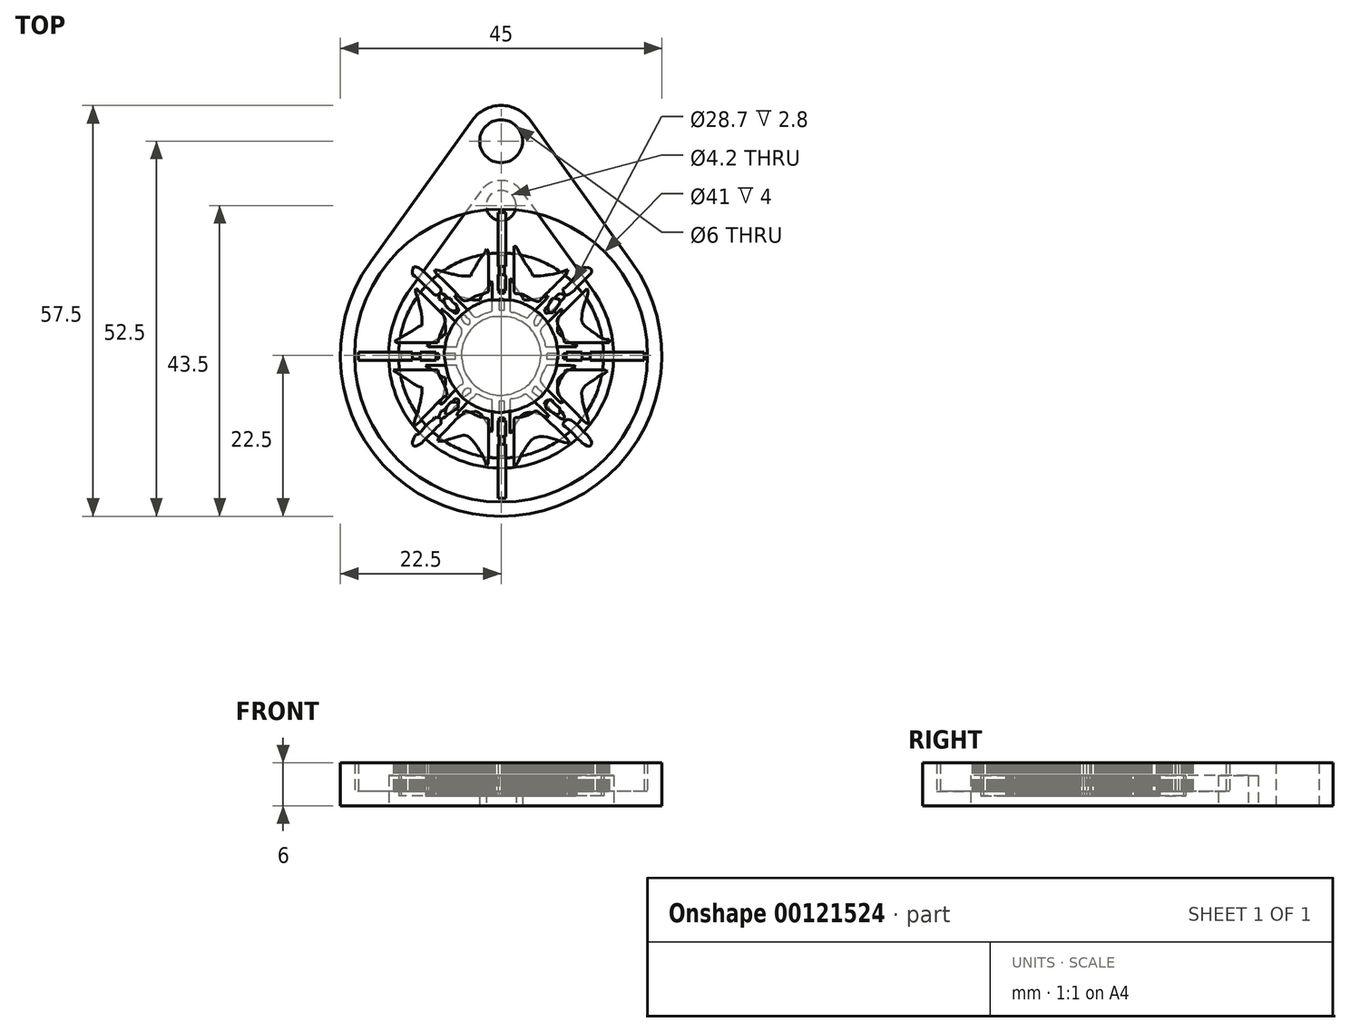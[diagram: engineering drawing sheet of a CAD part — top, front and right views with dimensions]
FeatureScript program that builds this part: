
annotation { "Feature Type Name" : "Feature", "Feature Type Description" : "" }
export const myFeature = defineFeature(function(context is Context, id is Id, definition is map)
    precondition{}
    {
        {
            var Q0;
            Q0=qCreatedBy(makeId("Top.planeOp"),FACE);
            var sketch = newSketch(context, id + "F0", { "sketchPlane" : qUnion([Q0])});
            skCircle(sketch, "E0", {"center": v(0, 0) * mm, "radius": 22.5 * mm});
            skCircle(sketch, "E1", {"center": v(0, 30) * mm, "radius": 5 * mm});
            skCircle(sketch, "E2", {"center": v(0, 30) * mm, "radius": 3 * mm});
            skLineSegment(sketch, "E3", {"start": v(-4.06, 32.92) * mm, "end": v(-18.28, 13.12) * mm});
            skLineSegment(sketch, "E4", {"start": v(4.06, 32.92) * mm, "end": v(18.28, 13.12) * mm});
            skCircle(sketch, "E5.0", {"center": v(0, 0) * mm, "radius": 20.5 * mm});
            skSolve(sketch);
        }
        {
            var Q0;
            Q0=makeQuery(id+"F0.imprint","IMPRINT",FACE,{"disambiguationData":[TD([[makeQuery(id+"F0.imprint","IMPRINT",EDGE,{"derivedFrom":sQuery(id+"F0.wireOp",EDGE,"E5.0")}),-1.0]])]});
            var Q1;
            {var subQ0=sQuery(id+"F0.wireOp",EDGE,"E3");Q1=makeQuery(id+"F0.imprint","IMPRINT",FACE,{"disambiguationData":[TD([[makeQuery(id+"F0.imprint","IMPRINT",EDGE,{"derivedFrom":subQ0}),1.0]])]});}
            var Q2;
            Q2=makeQuery(id+"F0.imprint","IMPRINT",FACE,{"disambiguationData":[TD([[makeQuery(id+"F0.imprint","IMPRINT",EDGE,{"derivedFrom":sQuery(id+"F0.wireOp",EDGE,"E2")}),-1.0]])]});
            extrude(context, id + "F1", {"entities" : qUnion([Q0, Q1, Q2]), "depth" : 6 * mm});
        }
        {
            var Q0;
            Q0=makeQuery(id+"F0.imprint","IMPRINT",FACE,{"disambiguationData":[TD([[makeQuery(id+"F0.imprint","IMPRINT",EDGE,{"derivedFrom":sQuery(id+"F0.wireOp",EDGE,"E5.0")}),1.0]])]});
            extrude(context, id + "F2", {"entities" : qUnion([Q0]), "operationType" : NewBodyOperationType.ADD, "depth" : 2 * mm});
        }
        {
            var Q0;
            Q0=makeQuery(id+"F2.opExtrude","CAP_FACE",FACE,{"disambiguationData":[OSD([sQuery(id+"F0.wireOp",EDGE,"E5.0")])],"isStart":false});
            var sketch = newSketch(context, id + "F3", { "sketchPlane" : qUnion([Q0])});
            skLineSegment(sketch, "E6", {"start": v(-0.44, 20) * mm, "end": v(-0.44, 12.44) * mm});
            skLineSegment(sketch, "E7", {"start": v(-0.44, 12.44) * mm, "end": v(0.67, 12.44) * mm});
            skLineSegment(sketch, "E8", {"start": v(0.67, 12.44) * mm, "end": v(0.67, 20) * mm});
            skLineSegment(sketch, "E9", {"start": v(0.67, 20) * mm, "end": v(-0.44, 20) * mm});
            skLineSegment(sketch, "E10", {"start": v(1.78, 15.33) * mm, "end": v(1.78, 8.89) * mm});
            skLineSegment(sketch, "E11", {"start": v(1.78, 8.89) * mm, "end": v(2, 8.67) * mm});
            skLineSegment(sketch, "E12", {"start": v(2, 8.67) * mm, "end": v(2.33, 8.66) * mm});
            skLineSegment(sketch, "E13", {"start": v(2.33, 8.66) * mm, "end": v(2.68, 8.62) * mm});
            skLineSegment(sketch, "E14", {"start": v(2.68, 8.62) * mm, "end": v(2.89, 8.57) * mm});
            skLineSegment(sketch, "E15", {"start": v(2.89, 8.57) * mm, "end": v(3.11, 8.5) * mm});
            skLineSegment(sketch, "E16", {"start": v(3.11, 8.5) * mm, "end": v(3.33, 8.42) * mm});
            skLineSegment(sketch, "E17", {"start": v(3.33, 8.42) * mm, "end": v(3.56, 8.3) * mm});
            skLineSegment(sketch, "E18", {"start": v(3.56, 8.3) * mm, "end": v(4, 8.04) * mm});
            skLineSegment(sketch, "E19", {"start": v(4, 8.04) * mm, "end": v(4.22, 7.91) * mm});
            skLineSegment(sketch, "E20", {"start": v(4.22, 7.91) * mm, "end": v(4.44, 7.8) * mm});
            skLineSegment(sketch, "E21", {"start": v(4.44, 7.8) * mm, "end": v(4.88, 7.65) * mm});
            skLineSegment(sketch, "E22", {"start": v(4.88, 7.65) * mm, "end": v(5, 7.61) * mm});
            skLineSegment(sketch, "E23", {"start": v(5, 7.61) * mm, "end": v(5.33, 7.56) * mm});
            skLineSegment(sketch, "E24", {"start": v(5.33, 7.56) * mm, "end": v(5.61, 7.88) * mm});
            skLineSegment(sketch, "E25", {"start": v(5.61, 7.88) * mm, "end": v(5.86, 8.19) * mm});
            skLineSegment(sketch, "E26", {"start": v(5.86, 8.19) * mm, "end": v(6, 8.35) * mm});
            skLineSegment(sketch, "E27", {"start": v(6, 8.35) * mm, "end": v(6.31, 8.67) * mm});
            skLineSegment(sketch, "E28", {"start": v(6.31, 8.67) * mm, "end": v(6.67, 8.98) * mm});
            skLineSegment(sketch, "E29", {"start": v(6.67, 8.98) * mm, "end": v(6.85, 9.15) * mm});
            skLineSegment(sketch, "E30", {"start": v(6.85, 9.15) * mm, "end": v(7.2, 9.51) * mm});
            skLineSegment(sketch, "E31", {"start": v(7.2, 9.51) * mm, "end": v(7.56, 9.86) * mm});
            skLineSegment(sketch, "E32", {"start": v(7.56, 9.86) * mm, "end": v(7.91, 10.22) * mm});
            skLineSegment(sketch, "E33", {"start": v(7.91, 10.22) * mm, "end": v(8.09, 10.4) * mm});
            skLineSegment(sketch, "E34", {"start": v(8.09, 10.4) * mm, "end": v(8.27, 10.58) * mm});
            skLineSegment(sketch, "E35", {"start": v(8.27, 10.58) * mm, "end": v(8.67, 10.94) * mm});
            skLineSegment(sketch, "E36", {"start": v(8.67, 10.94) * mm, "end": v(8.86, 11.13) * mm});
            skLineSegment(sketch, "E37", {"start": v(8.86, 11.13) * mm, "end": v(9.04, 11.33) * mm});
            skLineSegment(sketch, "E38", {"start": v(9.04, 11.33) * mm, "end": v(9.25, 11.67) * mm});
            skLineSegment(sketch, "E39", {"start": v(9.25, 11.67) * mm, "end": v(9.33, 12) * mm});
            skLineSegment(sketch, "E40", {"start": v(9.33, 12) * mm, "end": v(9, 11.9) * mm});
            skLineSegment(sketch, "E41", {"start": v(9, 11.9) * mm, "end": v(8.88, 11.85) * mm});
            skLineSegment(sketch, "E42", {"start": v(8.88, 11.85) * mm, "end": v(8.65, 11.78) * mm});
            skLineSegment(sketch, "E43", {"start": v(8.65, 11.78) * mm, "end": v(8.22, 11.64) * mm});
            skLineSegment(sketch, "E44", {"start": v(8.22, 11.64) * mm, "end": v(8, 11.59) * mm});
            skLineSegment(sketch, "E45", {"start": v(8, 11.59) * mm, "end": v(7.78, 11.52) * mm});
            skLineSegment(sketch, "E46", {"start": v(7.78, 11.52) * mm, "end": v(7.33, 11.42) * mm});
            skLineSegment(sketch, "E47", {"start": v(7.33, 11.42) * mm, "end": v(6.89, 11.35) * mm});
            skLineSegment(sketch, "E48", {"start": v(6.89, 11.35) * mm, "end": v(6.67, 11.32) * mm});
            skLineSegment(sketch, "E49", {"start": v(6.67, 11.32) * mm, "end": v(6.44, 11.28) * mm});
            skLineSegment(sketch, "E50", {"start": v(6.44, 11.28) * mm, "end": v(6.22, 11.25) * mm});
            skLineSegment(sketch, "E51", {"start": v(6.22, 11.25) * mm, "end": v(6, 11.2) * mm});
            skLineSegment(sketch, "E52", {"start": v(6, 11.2) * mm, "end": v(5.56, 11.13) * mm});
            skLineSegment(sketch, "E53", {"start": v(5.56, 11.13) * mm, "end": v(5.33, 11.12) * mm});
            skLineSegment(sketch, "E54", {"start": v(5.33, 11.12) * mm, "end": v(4.9, 11.11) * mm});
            skLineSegment(sketch, "E55", {"start": v(4.9, 11.11) * mm, "end": v(4.44, 11.11) * mm});
            skLineSegment(sketch, "E56", {"start": v(4.44, 11.11) * mm, "end": v(4.36, 11.44) * mm});
            skLineSegment(sketch, "E57", {"start": v(4.36, 11.44) * mm, "end": v(4.3, 11.57) * mm});
            skLineSegment(sketch, "E58", {"start": v(4.3, 11.57) * mm, "end": v(4.17, 11.8) * mm});
            skLineSegment(sketch, "E59", {"start": v(4.17, 11.8) * mm, "end": v(3.88, 12.22) * mm});
            skLineSegment(sketch, "E60", {"start": v(3.88, 12.22) * mm, "end": v(3.74, 12.43) * mm});
            skLineSegment(sketch, "E61", {"start": v(3.74, 12.43) * mm, "end": v(3.48, 12.8) * mm});
            skLineSegment(sketch, "E62", {"start": v(3.48, 12.8) * mm, "end": v(3.35, 12.98) * mm});
            skLineSegment(sketch, "E63", {"start": v(3.35, 12.98) * mm, "end": v(3.11, 13.35) * mm});
            skLineSegment(sketch, "E64", {"start": v(3.11, 13.35) * mm, "end": v(2.88, 13.78) * mm});
            skLineSegment(sketch, "E65", {"start": v(2.88, 13.78) * mm, "end": v(2.75, 14) * mm});
            skLineSegment(sketch, "E66", {"start": v(2.75, 14) * mm, "end": v(2.5, 14.44) * mm});
            skLineSegment(sketch, "E67", {"start": v(2.5, 14.44) * mm, "end": v(2.3, 14.86) * mm});
            skLineSegment(sketch, "E68", {"start": v(2.3, 14.86) * mm, "end": v(2.22, 15.04) * mm});
            skLineSegment(sketch, "E69", {"start": v(2.22, 15.04) * mm, "end": v(2.1, 15.17) * mm});
            skLineSegment(sketch, "E70", {"start": v(2.1, 15.17) * mm, "end": v(2.04, 15.25) * mm});
            skLineSegment(sketch, "E71", {"start": v(2.04, 15.25) * mm, "end": v(1.78, 15.33) * mm});
            skLineSegment(sketch, "E72", {"start": v(-2, 14.89) * mm, "end": v(-2.22, 14.56) * mm});
            skLineSegment(sketch, "E73", {"start": v(-2.22, 14.56) * mm, "end": v(-2.28, 14.44) * mm});
            skLineSegment(sketch, "E74", {"start": v(-2.28, 14.44) * mm, "end": v(-2.53, 14.05) * mm});
            skLineSegment(sketch, "E75", {"start": v(-2.53, 14.05) * mm, "end": v(-2.8, 13.7) * mm});
            skLineSegment(sketch, "E76", {"start": v(-2.8, 13.7) * mm, "end": v(-3.07, 13.31) * mm});
            skLineSegment(sketch, "E77", {"start": v(-3.07, 13.31) * mm, "end": v(-3.2, 13.1) * mm});
            skLineSegment(sketch, "E78", {"start": v(-3.2, 13.1) * mm, "end": v(-3.32, 12.89) * mm});
            skLineSegment(sketch, "E79", {"start": v(-3.32, 12.89) * mm, "end": v(-3.56, 12.46) * mm});
            skLineSegment(sketch, "E80", {"start": v(-3.56, 12.46) * mm, "end": v(-3.8, 12.09) * mm});
            skLineSegment(sketch, "E81", {"start": v(-3.8, 12.09) * mm, "end": v(-4.02, 11.74) * mm});
            skLineSegment(sketch, "E82", {"start": v(-4.02, 11.74) * mm, "end": v(-4.16, 11.44) * mm});
            skLineSegment(sketch, "E83", {"start": v(-4.16, 11.44) * mm, "end": v(-4.22, 11.11) * mm});
            skLineSegment(sketch, "E84", {"start": v(-4.22, 11.11) * mm, "end": v(-4.9, 11.11) * mm});
            skLineSegment(sketch, "E85", {"start": v(-4.9, 11.11) * mm, "end": v(-5.11, 11.11) * mm});
            skLineSegment(sketch, "E86", {"start": v(-5.11, 11.11) * mm, "end": v(-5.56, 11.13) * mm});
            skLineSegment(sketch, "E87", {"start": v(-5.56, 11.13) * mm, "end": v(-6, 11.2) * mm});
            skLineSegment(sketch, "E88", {"start": v(-6, 11.2) * mm, "end": v(-6.22, 11.25) * mm});
            skLineSegment(sketch, "E89", {"start": v(-6.22, 11.25) * mm, "end": v(-6.67, 11.36) * mm});
            skLineSegment(sketch, "E90", {"start": v(-6.67, 11.36) * mm, "end": v(-6.89, 11.41) * mm});
            skLineSegment(sketch, "E91", {"start": v(-6.89, 11.41) * mm, "end": v(-7.11, 11.48) * mm});
            skLineSegment(sketch, "E92", {"start": v(-7.11, 11.48) * mm, "end": v(-7.33, 11.52) * mm});
            skLineSegment(sketch, "E93", {"start": v(-7.33, 11.52) * mm, "end": v(-7.78, 11.64) * mm});
            skLineSegment(sketch, "E94", {"start": v(-7.78, 11.64) * mm, "end": v(-8, 11.7) * mm});
            skLineSegment(sketch, "E95", {"start": v(-8, 11.7) * mm, "end": v(-8.44, 11.85) * mm});
            skLineSegment(sketch, "E96", {"start": v(-8.44, 11.85) * mm, "end": v(-8.65, 11.9) * mm});
            skLineSegment(sketch, "E97", {"start": v(-8.65, 11.9) * mm, "end": v(-9, 11.98) * mm});
            skLineSegment(sketch, "E98", {"start": v(-9, 11.98) * mm, "end": v(-9.33, 12) * mm});
            skLineSegment(sketch, "E99", {"start": v(-9.33, 12) * mm, "end": v(-9.25, 11.72) * mm});
            skLineSegment(sketch, "E100", {"start": v(-9.25, 11.72) * mm, "end": v(-9.17, 11.63) * mm});
            skLineSegment(sketch, "E101", {"start": v(-9.17, 11.63) * mm, "end": v(-9.04, 11.46) * mm});
            skLineSegment(sketch, "E102", {"start": v(-9.04, 11.46) * mm, "end": v(-8.66, 11.1) * mm});
            skLineSegment(sketch, "E103", {"start": v(-8.66, 11.1) * mm, "end": v(-8.22, 10.67) * mm});
            skLineSegment(sketch, "E104", {"start": v(-8.22, 10.67) * mm, "end": v(-7.78, 10.22) * mm});
            skLineSegment(sketch, "E105", {"start": v(-7.78, 10.22) * mm, "end": v(-7.11, 9.56) * mm});
            skLineSegment(sketch, "E106", {"start": v(-7.11, 9.56) * mm, "end": v(-6.67, 9.11) * mm});
            skLineSegment(sketch, "E107", {"start": v(-6.67, 9.11) * mm, "end": v(-6.45, 8.89) * mm});
            skLineSegment(sketch, "E108", {"start": v(-6.45, 8.89) * mm, "end": v(-6.24, 8.67) * mm});
            skLineSegment(sketch, "E109", {"start": v(-6.24, 8.67) * mm, "end": v(-5.86, 8.23) * mm});
            skLineSegment(sketch, "E110", {"start": v(-5.86, 8.23) * mm, "end": v(-5.7, 8.02) * mm});
            skLineSegment(sketch, "E111", {"start": v(-5.7, 8.02) * mm, "end": v(-5.5, 7.85) * mm});
            skLineSegment(sketch, "E112", {"start": v(-5.5, 7.85) * mm, "end": v(-5.1, 7.65) * mm});
            skLineSegment(sketch, "E113", {"start": v(-5.1, 7.65) * mm, "end": v(-4.67, 7.72) * mm});
            skLineSegment(sketch, "E114", {"start": v(-4.67, 7.72) * mm, "end": v(-4.44, 7.83) * mm});
            skLineSegment(sketch, "E115", {"start": v(-4.44, 7.83) * mm, "end": v(-4, 8.12) * mm});
            skLineSegment(sketch, "E116", {"start": v(-4, 8.12) * mm, "end": v(-3.78, 8.23) * mm});
            skLineSegment(sketch, "E117", {"start": v(-3.78, 8.23) * mm, "end": v(-3.56, 8.34) * mm});
            skLineSegment(sketch, "E118", {"start": v(-3.56, 8.34) * mm, "end": v(-3.11, 8.48) * mm});
            skLineSegment(sketch, "E119", {"start": v(-3.11, 8.48) * mm, "end": v(-2.89, 8.53) * mm});
            skLineSegment(sketch, "E120", {"start": v(-2.89, 8.53) * mm, "end": v(-2.67, 8.6) * mm});
            skLineSegment(sketch, "E121", {"start": v(-2.67, 8.6) * mm, "end": v(-2.23, 8.74) * mm});
            skLineSegment(sketch, "E122", {"start": v(-2.23, 8.74) * mm, "end": v(-2.11, 8.8) * mm});
            skLineSegment(sketch, "E123", {"start": v(-2.11, 8.8) * mm, "end": v(-1.78, 8.89) * mm});
            skLineSegment(sketch, "E124", {"start": v(-1.78, 8.89) * mm, "end": v(-1.78, 12.89) * mm});
            skLineSegment(sketch, "E125", {"start": v(-1.78, 12.89) * mm, "end": v(-1.78, 13.56) * mm});
            skLineSegment(sketch, "E126", {"start": v(-1.78, 13.56) * mm, "end": v(-1.78, 13.78) * mm});
            skLineSegment(sketch, "E127", {"start": v(-1.78, 13.78) * mm, "end": v(-1.78, 14.22) * mm});
            skLineSegment(sketch, "E128", {"start": v(-1.78, 14.22) * mm, "end": v(-1.8, 14.42) * mm});
            skLineSegment(sketch, "E129", {"start": v(-1.8, 14.42) * mm, "end": v(-1.83, 14.6) * mm});
            skLineSegment(sketch, "E130", {"start": v(-1.83, 14.6) * mm, "end": v(-1.84, 14.72) * mm});
            skLineSegment(sketch, "E131", {"start": v(-1.84, 14.72) * mm, "end": v(-2, 14.89) * mm});
            skLineSegment(sketch, "E132", {"start": v(-12.22, 12.44) * mm, "end": v(-12.38, 12.11) * mm});
            skLineSegment(sketch, "E133", {"start": v(-12.38, 12.11) * mm, "end": v(-12.39, 12) * mm});
            skLineSegment(sketch, "E134", {"start": v(-12.39, 12) * mm, "end": v(-12.43, 11.78) * mm});
            skLineSegment(sketch, "E135", {"start": v(-12.43, 11.78) * mm, "end": v(-12.44, 11.33) * mm});
            skLineSegment(sketch, "E136", {"start": v(-12.44, 11.33) * mm, "end": v(-12.11, 11.16) * mm});
            skLineSegment(sketch, "E137", {"start": v(-12.11, 11.16) * mm, "end": v(-11.99, 11.04) * mm});
            skLineSegment(sketch, "E138", {"start": v(-11.99, 11.04) * mm, "end": v(-11.77, 10.86) * mm});
            skLineSegment(sketch, "E139", {"start": v(-11.77, 10.86) * mm, "end": v(-11.56, 10.66) * mm});
            skLineSegment(sketch, "E140", {"start": v(-11.56, 10.66) * mm, "end": v(-11.33, 10.44) * mm});
            skLineSegment(sketch, "E141", {"start": v(-11.33, 10.44) * mm, "end": v(-10.89, 10) * mm});
            skLineSegment(sketch, "E142", {"start": v(-10.89, 10) * mm, "end": v(-10.44, 9.56) * mm});
            skLineSegment(sketch, "E143", {"start": v(-10.44, 9.56) * mm, "end": v(-9.33, 8.44) * mm});
            skLineSegment(sketch, "E144", {"start": v(-9.33, 8.44) * mm, "end": v(-8.89, 8.44) * mm});
            skLineSegment(sketch, "E145", {"start": v(-8.89, 8.44) * mm, "end": v(-8.44, 8.89) * mm});
            skLineSegment(sketch, "E146", {"start": v(-8.44, 8.89) * mm, "end": v(-8.44, 9.33) * mm});
            skLineSegment(sketch, "E147", {"start": v(-8.44, 9.33) * mm, "end": v(-9.56, 10.44) * mm});
            skLineSegment(sketch, "E148", {"start": v(-9.56, 10.44) * mm, "end": v(-10, 10.89) * mm});
            skLineSegment(sketch, "E149", {"start": v(-10, 10.89) * mm, "end": v(-10.22, 11.11) * mm});
            skLineSegment(sketch, "E150", {"start": v(-10.22, 11.11) * mm, "end": v(-10.67, 11.56) * mm});
            skLineSegment(sketch, "E151", {"start": v(-10.67, 11.56) * mm, "end": v(-10.89, 11.77) * mm});
            skLineSegment(sketch, "E152", {"start": v(-10.89, 11.77) * mm, "end": v(-11.11, 11.98) * mm});
            skLineSegment(sketch, "E153", {"start": v(-11.11, 11.98) * mm, "end": v(-11.54, 12.28) * mm});
            skLineSegment(sketch, "E154", {"start": v(-11.54, 12.28) * mm, "end": v(-11.89, 12.42) * mm});
            skLineSegment(sketch, "E155", {"start": v(-11.89, 12.42) * mm, "end": v(-12.22, 12.44) * mm});
            skLineSegment(sketch, "E156", {"start": v(8.67, 9.33) * mm, "end": v(8.72, 8.89) * mm});
            skLineSegment(sketch, "E157", {"start": v(8.72, 8.89) * mm, "end": v(8.73, 8.77) * mm});
            skLineSegment(sketch, "E158", {"start": v(8.73, 8.77) * mm, "end": v(8.89, 8.44) * mm});
            skLineSegment(sketch, "E159", {"start": v(8.89, 8.44) * mm, "end": v(9.22, 8.47) * mm});
            skLineSegment(sketch, "E160", {"start": v(9.22, 8.47) * mm, "end": v(9.57, 8.6) * mm});
            skLineSegment(sketch, "E161", {"start": v(9.57, 8.6) * mm, "end": v(10, 8.91) * mm});
            skLineSegment(sketch, "E162", {"start": v(10, 8.91) * mm, "end": v(10.22, 9.12) * mm});
            skLineSegment(sketch, "E163", {"start": v(10.22, 9.12) * mm, "end": v(10.44, 9.33) * mm});
            skLineSegment(sketch, "E164", {"start": v(10.44, 9.33) * mm, "end": v(10.89, 9.78) * mm});
            skLineSegment(sketch, "E165", {"start": v(10.89, 9.78) * mm, "end": v(11.11, 10) * mm});
            skLineSegment(sketch, "E166", {"start": v(11.11, 10) * mm, "end": v(11.56, 10.44) * mm});
            skLineSegment(sketch, "E167", {"start": v(11.56, 10.44) * mm, "end": v(12.67, 11.56) * mm});
            skLineSegment(sketch, "E168", {"start": v(12.67, 11.56) * mm, "end": v(12.67, 12) * mm});
            skLineSegment(sketch, "E169", {"start": v(12.67, 12) * mm, "end": v(12.33, 12.25) * mm});
            skLineSegment(sketch, "E170", {"start": v(12.33, 12.25) * mm, "end": v(12.2, 12.3) * mm});
            skLineSegment(sketch, "E171", {"start": v(12.2, 12.3) * mm, "end": v(11.78, 12.35) * mm});
            skLineSegment(sketch, "E172", {"start": v(11.78, 12.35) * mm, "end": v(11.57, 12.28) * mm});
            skLineSegment(sketch, "E173", {"start": v(11.57, 12.28) * mm, "end": v(11.38, 12.15) * mm});
            skLineSegment(sketch, "E174", {"start": v(11.38, 12.15) * mm, "end": v(11.02, 11.82) * mm});
            skLineSegment(sketch, "E175", {"start": v(11.02, 11.82) * mm, "end": v(10.85, 11.64) * mm});
            skLineSegment(sketch, "E176", {"start": v(10.85, 11.64) * mm, "end": v(10.5, 11.28) * mm});
            skLineSegment(sketch, "E177", {"start": v(10.5, 11.28) * mm, "end": v(10.22, 10.89) * mm});
            skLineSegment(sketch, "E178", {"start": v(10.22, 10.89) * mm, "end": v(10.09, 10.69) * mm});
            skLineSegment(sketch, "E179", {"start": v(10.09, 10.69) * mm, "end": v(9.94, 10.5) * mm});
            skLineSegment(sketch, "E180", {"start": v(9.94, 10.5) * mm, "end": v(9.77, 10.3) * mm});
            skLineSegment(sketch, "E181", {"start": v(9.77, 10.3) * mm, "end": v(9.42, 9.96) * mm});
            skLineSegment(sketch, "E182", {"start": v(9.42, 9.96) * mm, "end": v(9.07, 9.62) * mm});
            skLineSegment(sketch, "E183", {"start": v(9.07, 9.62) * mm, "end": v(8.98, 9.5) * mm});
            skLineSegment(sketch, "E184", {"start": v(8.98, 9.5) * mm, "end": v(8.67, 9.33) * mm});
            skLineSegment(sketch, "E185", {"start": v(-0.44, 11.33) * mm, "end": v(-0.44, 9.11) * mm});
            skLineSegment(sketch, "E186", {"start": v(-0.44, 9.11) * mm, "end": v(0.67, 9.11) * mm});
            skLineSegment(sketch, "E187", {"start": v(0.67, 9.11) * mm, "end": v(0.67, 11.11) * mm});
            skLineSegment(sketch, "E188", {"start": v(0.67, 11.11) * mm, "end": v(0.44, 11.33) * mm});
            skLineSegment(sketch, "E189", {"start": v(0.44, 11.33) * mm, "end": v(-0.44, 11.33) * mm});
            skLineSegment(sketch, "E190", {"start": v(-12, 9.33) * mm, "end": v(-11.98, 9) * mm});
            skLineSegment(sketch, "E191", {"start": v(-11.98, 9) * mm, "end": v(-11.9, 8.65) * mm});
            skLineSegment(sketch, "E192", {"start": v(-11.9, 8.65) * mm, "end": v(-11.74, 8.22) * mm});
            skLineSegment(sketch, "E193", {"start": v(-11.74, 8.22) * mm, "end": v(-11.66, 8) * mm});
            skLineSegment(sketch, "E194", {"start": v(-11.66, 8) * mm, "end": v(-11.56, 7.56) * mm});
            skLineSegment(sketch, "E195", {"start": v(-11.56, 7.56) * mm, "end": v(-11.46, 7.11) * mm});
            skLineSegment(sketch, "E196", {"start": v(-11.46, 7.11) * mm, "end": v(-11.4, 6.89) * mm});
            skLineSegment(sketch, "E197", {"start": v(-11.4, 6.89) * mm, "end": v(-11.27, 6.44) * mm});
            skLineSegment(sketch, "E198", {"start": v(-11.27, 6.44) * mm, "end": v(-11.2, 6.22) * mm});
            skLineSegment(sketch, "E199", {"start": v(-11.2, 6.22) * mm, "end": v(-11.13, 5.78) * mm});
            skLineSegment(sketch, "E200", {"start": v(-11.13, 5.78) * mm, "end": v(-11.11, 5.33) * mm});
            skLineSegment(sketch, "E201", {"start": v(-11.11, 5.33) * mm, "end": v(-11.11, 5.11) * mm});
            skLineSegment(sketch, "E202", {"start": v(-11.11, 5.11) * mm, "end": v(-11.11, 4.9) * mm});
            skLineSegment(sketch, "E203", {"start": v(-11.11, 4.9) * mm, "end": v(-11.11, 4.22) * mm});
            skLineSegment(sketch, "E204", {"start": v(-11.11, 4.22) * mm, "end": v(-11.44, 4.1) * mm});
            skLineSegment(sketch, "E205", {"start": v(-11.44, 4.1) * mm, "end": v(-11.57, 4.02) * mm});
            skLineSegment(sketch, "E206", {"start": v(-11.57, 4.02) * mm, "end": v(-11.8, 3.9) * mm});
            skLineSegment(sketch, "E207", {"start": v(-11.8, 3.9) * mm, "end": v(-12.22, 3.6) * mm});
            skLineSegment(sketch, "E208", {"start": v(-12.22, 3.6) * mm, "end": v(-12.44, 3.44) * mm});
            skLineSegment(sketch, "E209", {"start": v(-12.44, 3.44) * mm, "end": v(-12.89, 3.2) * mm});
            skLineSegment(sketch, "E210", {"start": v(-12.89, 3.2) * mm, "end": v(-13.33, 2.98) * mm});
            skLineSegment(sketch, "E211", {"start": v(-13.33, 2.98) * mm, "end": v(-13.78, 2.7) * mm});
            skLineSegment(sketch, "E212", {"start": v(-13.78, 2.7) * mm, "end": v(-14, 2.54) * mm});
            skLineSegment(sketch, "E213", {"start": v(-14, 2.54) * mm, "end": v(-14.43, 2.28) * mm});
            skLineSegment(sketch, "E214", {"start": v(-14.43, 2.28) * mm, "end": v(-14.56, 2.22) * mm});
            skLineSegment(sketch, "E215", {"start": v(-14.56, 2.22) * mm, "end": v(-14.89, 2) * mm});
            skLineSegment(sketch, "E216", {"start": v(-14.89, 2) * mm, "end": v(-14.72, 1.84) * mm});
            skLineSegment(sketch, "E217", {"start": v(-14.72, 1.84) * mm, "end": v(-14.6, 1.83) * mm});
            skLineSegment(sketch, "E218", {"start": v(-14.6, 1.83) * mm, "end": v(-14.42, 1.8) * mm});
            skLineSegment(sketch, "E219", {"start": v(-14.42, 1.8) * mm, "end": v(-14.22, 1.78) * mm});
            skLineSegment(sketch, "E220", {"start": v(-14.22, 1.78) * mm, "end": v(-13.78, 1.78) * mm});
            skLineSegment(sketch, "E221", {"start": v(-13.78, 1.78) * mm, "end": v(-13.56, 1.78) * mm});
            skLineSegment(sketch, "E222", {"start": v(-13.56, 1.78) * mm, "end": v(-12.89, 1.78) * mm});
            skLineSegment(sketch, "E223", {"start": v(-12.89, 1.78) * mm, "end": v(-8.89, 1.78) * mm});
            skLineSegment(sketch, "E224", {"start": v(-8.89, 1.78) * mm, "end": v(-8.75, 2.23) * mm});
            skLineSegment(sketch, "E225", {"start": v(-8.75, 2.23) * mm, "end": v(-8.7, 2.46) * mm});
            skLineSegment(sketch, "E226", {"start": v(-8.7, 2.46) * mm, "end": v(-8.57, 2.89) * mm});
            skLineSegment(sketch, "E227", {"start": v(-8.57, 2.89) * mm, "end": v(-8.39, 3.33) * mm});
            skLineSegment(sketch, "E228", {"start": v(-8.39, 3.33) * mm, "end": v(-8.27, 3.56) * mm});
            skLineSegment(sketch, "E229", {"start": v(-8.27, 3.56) * mm, "end": v(-8.17, 3.78) * mm});
            skLineSegment(sketch, "E230", {"start": v(-8.17, 3.78) * mm, "end": v(-7.97, 4.22) * mm});
            skLineSegment(sketch, "E231", {"start": v(-7.97, 4.22) * mm, "end": v(-7.88, 4.44) * mm});
            skLineSegment(sketch, "E232", {"start": v(-7.88, 4.44) * mm, "end": v(-7.81, 4.89) * mm});
            skLineSegment(sketch, "E233", {"start": v(-7.81, 4.89) * mm, "end": v(-7.89, 5.31) * mm});
            skLineSegment(sketch, "E234", {"start": v(-7.89, 5.31) * mm, "end": v(-8.11, 5.7) * mm});
            skLineSegment(sketch, "E235", {"start": v(-8.11, 5.7) * mm, "end": v(-8.46, 6.05) * mm});
            skLineSegment(sketch, "E236", {"start": v(-8.46, 6.05) * mm, "end": v(-8.67, 6.24) * mm});
            skLineSegment(sketch, "E237", {"start": v(-8.67, 6.24) * mm, "end": v(-8.89, 6.45) * mm});
            skLineSegment(sketch, "E238", {"start": v(-8.89, 6.45) * mm, "end": v(-9.11, 6.67) * mm});
            skLineSegment(sketch, "E239", {"start": v(-9.11, 6.67) * mm, "end": v(-9.56, 7.11) * mm});
            skLineSegment(sketch, "E240", {"start": v(-9.56, 7.11) * mm, "end": v(-10.22, 7.78) * mm});
            skLineSegment(sketch, "E241", {"start": v(-10.22, 7.78) * mm, "end": v(-10.44, 8) * mm});
            skLineSegment(sketch, "E242", {"start": v(-10.44, 8) * mm, "end": v(-10.89, 8.44) * mm});
            skLineSegment(sketch, "E243", {"start": v(-10.89, 8.44) * mm, "end": v(-11.11, 8.66) * mm});
            skLineSegment(sketch, "E244", {"start": v(-11.11, 8.66) * mm, "end": v(-11.32, 8.86) * mm});
            skLineSegment(sketch, "E245", {"start": v(-11.32, 8.86) * mm, "end": v(-11.54, 9.04) * mm});
            skLineSegment(sketch, "E246", {"start": v(-11.54, 9.04) * mm, "end": v(-11.67, 9.16) * mm});
            skLineSegment(sketch, "E247", {"start": v(-11.67, 9.16) * mm, "end": v(-12, 9.33) * mm});
            skLineSegment(sketch, "E248", {"start": v(12, 9.33) * mm, "end": v(10, 7.33) * mm});
            skLineSegment(sketch, "E249", {"start": v(10, 7.33) * mm, "end": v(9.33, 6.67) * mm});
            skLineSegment(sketch, "E250", {"start": v(9.33, 6.67) * mm, "end": v(9.11, 6.44) * mm});
            skLineSegment(sketch, "E251", {"start": v(9.11, 6.44) * mm, "end": v(8.67, 6.02) * mm});
            skLineSegment(sketch, "E252", {"start": v(8.67, 6.02) * mm, "end": v(8.28, 5.64) * mm});
            skLineSegment(sketch, "E253", {"start": v(8.28, 5.64) * mm, "end": v(8.11, 5.47) * mm});
            skLineSegment(sketch, "E254", {"start": v(8.11, 5.47) * mm, "end": v(7.9, 5.1) * mm});
            skLineSegment(sketch, "E255", {"start": v(7.9, 5.1) * mm, "end": v(7.85, 4.88) * mm});
            skLineSegment(sketch, "E256", {"start": v(7.85, 4.88) * mm, "end": v(7.9, 4.44) * mm});
            skLineSegment(sketch, "E257", {"start": v(7.9, 4.44) * mm, "end": v(7.98, 4.22) * mm});
            skLineSegment(sketch, "E258", {"start": v(7.98, 4.22) * mm, "end": v(8.22, 3.78) * mm});
            skLineSegment(sketch, "E259", {"start": v(8.22, 3.78) * mm, "end": v(8.46, 3.33) * mm});
            skLineSegment(sketch, "E260", {"start": v(8.46, 3.33) * mm, "end": v(8.56, 3.11) * mm});
            skLineSegment(sketch, "E261", {"start": v(8.56, 3.11) * mm, "end": v(8.62, 2.89) * mm});
            skLineSegment(sketch, "E262", {"start": v(8.62, 2.89) * mm, "end": v(8.7, 2.46) * mm});
            skLineSegment(sketch, "E263", {"start": v(8.7, 2.46) * mm, "end": v(8.76, 2.23) * mm});
            skLineSegment(sketch, "E264", {"start": v(8.76, 2.23) * mm, "end": v(8.89, 1.78) * mm});
            skLineSegment(sketch, "E265", {"start": v(8.89, 1.78) * mm, "end": v(15.11, 1.78) * mm});
            skLineSegment(sketch, "E266", {"start": v(15.11, 1.78) * mm, "end": v(15.11, 2.22) * mm});
            skLineSegment(sketch, "E267", {"start": v(15.11, 2.22) * mm, "end": v(14.78, 2.24) * mm});
            skLineSegment(sketch, "E268", {"start": v(14.78, 2.24) * mm, "end": v(14.43, 2.33) * mm});
            skLineSegment(sketch, "E269", {"start": v(14.43, 2.33) * mm, "end": v(14, 2.5) * mm});
            skLineSegment(sketch, "E270", {"start": v(14, 2.5) * mm, "end": v(13.56, 2.77) * mm});
            skLineSegment(sketch, "E271", {"start": v(13.56, 2.77) * mm, "end": v(13.33, 2.93) * mm});
            skLineSegment(sketch, "E272", {"start": v(13.33, 2.93) * mm, "end": v(12.89, 3.25) * mm});
            skLineSegment(sketch, "E273", {"start": v(12.89, 3.25) * mm, "end": v(12.67, 3.41) * mm});
            skLineSegment(sketch, "E274", {"start": v(12.67, 3.41) * mm, "end": v(12.44, 3.59) * mm});
            skLineSegment(sketch, "E275", {"start": v(12.44, 3.59) * mm, "end": v(12, 3.92) * mm});
            skLineSegment(sketch, "E276", {"start": v(12, 3.92) * mm, "end": v(11.78, 4.09) * mm});
            skLineSegment(sketch, "E277", {"start": v(11.78, 4.09) * mm, "end": v(11.43, 4.46) * mm});
            skLineSegment(sketch, "E278", {"start": v(11.43, 4.46) * mm, "end": v(11.32, 4.67) * mm});
            skLineSegment(sketch, "E279", {"start": v(11.32, 4.67) * mm, "end": v(11.27, 5.11) * mm});
            skLineSegment(sketch, "E280", {"start": v(11.27, 5.11) * mm, "end": v(11.32, 5.56) * mm});
            skLineSegment(sketch, "E281", {"start": v(11.32, 5.56) * mm, "end": v(11.35, 5.78) * mm});
            skLineSegment(sketch, "E282", {"start": v(11.35, 5.78) * mm, "end": v(11.42, 6.22) * mm});
            skLineSegment(sketch, "E283", {"start": v(11.42, 6.22) * mm, "end": v(11.47, 6.44) * mm});
            skLineSegment(sketch, "E284", {"start": v(11.47, 6.44) * mm, "end": v(11.51, 6.67) * mm});
            skLineSegment(sketch, "E285", {"start": v(11.51, 6.67) * mm, "end": v(11.62, 7.11) * mm});
            skLineSegment(sketch, "E286", {"start": v(11.62, 7.11) * mm, "end": v(11.78, 7.56) * mm});
            skLineSegment(sketch, "E287", {"start": v(11.78, 7.56) * mm, "end": v(11.87, 7.78) * mm});
            skLineSegment(sketch, "E288", {"start": v(11.87, 7.78) * mm, "end": v(12.02, 8.22) * mm});
            skLineSegment(sketch, "E289", {"start": v(12.02, 8.22) * mm, "end": v(12.13, 8.66) * mm});
            skLineSegment(sketch, "E290", {"start": v(12.13, 8.66) * mm, "end": v(12.16, 8.86) * mm});
            skLineSegment(sketch, "E291", {"start": v(12.16, 8.86) * mm, "end": v(12.15, 9.04) * mm});
            skLineSegment(sketch, "E292", {"start": v(12.15, 9.04) * mm, "end": v(12.15, 9.16) * mm});
            skLineSegment(sketch, "E293", {"start": v(12.15, 9.16) * mm, "end": v(12, 9.33) * mm});
            skLineSegment(sketch, "E294", {"start": v(-8, 8) * mm, "end": v(-7.98, 7.54) * mm});
            skLineSegment(sketch, "E295", {"start": v(-7.98, 7.54) * mm, "end": v(-7.93, 7.32) * mm});
            skLineSegment(sketch, "E296", {"start": v(-7.93, 7.32) * mm, "end": v(-7.84, 7.11) * mm});
            skLineSegment(sketch, "E297", {"start": v(-7.84, 7.11) * mm, "end": v(-7.53, 6.7) * mm});
            skLineSegment(sketch, "E298", {"start": v(-7.53, 6.7) * mm, "end": v(-7.12, 6.38) * mm});
            skLineSegment(sketch, "E299", {"start": v(-7.12, 6.38) * mm, "end": v(-6.78, 6.25) * mm});
            skLineSegment(sketch, "E300", {"start": v(-6.78, 6.25) * mm, "end": v(-6.44, 6.22) * mm});
            skLineSegment(sketch, "E301", {"start": v(-6.44, 6.22) * mm, "end": v(-6.22, 6.44) * mm});
            skLineSegment(sketch, "E302", {"start": v(-6.22, 6.44) * mm, "end": v(-6.22, 7.11) * mm});
            skLineSegment(sketch, "E303", {"start": v(-6.22, 7.11) * mm, "end": v(-6.5, 7.27) * mm});
            skLineSegment(sketch, "E304", {"start": v(-6.5, 7.27) * mm, "end": v(-6.59, 7.35) * mm});
            skLineSegment(sketch, "E305", {"start": v(-6.59, 7.35) * mm, "end": v(-6.74, 7.48) * mm});
            skLineSegment(sketch, "E306", {"start": v(-6.74, 7.48) * mm, "end": v(-6.96, 7.72) * mm});
            skLineSegment(sketch, "E307", {"start": v(-6.96, 7.72) * mm, "end": v(-7.11, 8) * mm});
            skLineSegment(sketch, "E308", {"start": v(-7.11, 8) * mm, "end": v(-8, 8) * mm});
            skLineSegment(sketch, "E309", {"start": v(7.11, 8) * mm, "end": v(6.96, 7.67) * mm});
            skLineSegment(sketch, "E310", {"start": v(6.96, 7.67) * mm, "end": v(6.75, 7.32) * mm});
            skLineSegment(sketch, "E311", {"start": v(6.75, 7.32) * mm, "end": v(6.57, 6.89) * mm});
            skLineSegment(sketch, "E312", {"start": v(6.57, 6.89) * mm, "end": v(6.55, 6.68) * mm});
            skLineSegment(sketch, "E313", {"start": v(6.55, 6.68) * mm, "end": v(6.56, 6.46) * mm});
            skLineSegment(sketch, "E314", {"start": v(6.56, 6.46) * mm, "end": v(6.67, 6) * mm});
            skLineSegment(sketch, "E315", {"start": v(6.67, 6) * mm, "end": v(7.33, 6) * mm});
            skLineSegment(sketch, "E316", {"start": v(7.33, 6) * mm, "end": v(7.5, 6.33) * mm});
            skLineSegment(sketch, "E317", {"start": v(7.5, 6.33) * mm, "end": v(7.62, 6.46) * mm});
            skLineSegment(sketch, "E318", {"start": v(7.62, 6.46) * mm, "end": v(7.78, 6.68) * mm});
            skLineSegment(sketch, "E319", {"start": v(7.78, 6.68) * mm, "end": v(8.06, 7.1) * mm});
            skLineSegment(sketch, "E320", {"start": v(8.06, 7.1) * mm, "end": v(8.2, 7.44) * mm});
            skLineSegment(sketch, "E321", {"start": v(8.2, 7.44) * mm, "end": v(8.22, 7.78) * mm});
            skLineSegment(sketch, "E322", {"start": v(8.22, 7.78) * mm, "end": v(7.89, 7.94) * mm});
            skLineSegment(sketch, "E323", {"start": v(7.89, 7.94) * mm, "end": v(7.78, 7.94) * mm});
            skLineSegment(sketch, "E324", {"start": v(7.78, 7.94) * mm, "end": v(7.56, 7.99) * mm});
            skLineSegment(sketch, "E325", {"start": v(7.56, 7.99) * mm, "end": v(7.11, 8) * mm});
            skLineSegment(sketch, "E326", {"start": v(-2.22, 7.67) * mm, "end": v(-2.67, 7.5) * mm});
            skLineSegment(sketch, "E327", {"start": v(-2.67, 7.5) * mm, "end": v(-2.89, 7.39) * mm});
            skLineSegment(sketch, "E328", {"start": v(-2.89, 7.39) * mm, "end": v(-3.11, 7.3) * mm});
            skLineSegment(sketch, "E329", {"start": v(-3.11, 7.3) * mm, "end": v(-3.33, 7.2) * mm});
            skLineSegment(sketch, "E330", {"start": v(-3.33, 7.2) * mm, "end": v(-3.56, 7.1) * mm});
            skLineSegment(sketch, "E331", {"start": v(-3.56, 7.1) * mm, "end": v(-4, 6.87) * mm});
            skLineSegment(sketch, "E332", {"start": v(-4, 6.87) * mm, "end": v(-4.44, 6.6) * mm});
            skLineSegment(sketch, "E333", {"start": v(-4.44, 6.6) * mm, "end": v(-4.65, 6.44) * mm});
            skLineSegment(sketch, "E334", {"start": v(-4.65, 6.44) * mm, "end": v(-5.02, 6.15) * mm});
            skLineSegment(sketch, "E335", {"start": v(-5.02, 6.15) * mm, "end": v(-5.38, 5.85) * mm});
            skLineSegment(sketch, "E336", {"start": v(-5.38, 5.85) * mm, "end": v(-5.77, 5.5) * mm});
            skLineSegment(sketch, "E337", {"start": v(-5.77, 5.5) * mm, "end": v(-5.95, 5.31) * mm});
            skLineSegment(sketch, "E338", {"start": v(-5.95, 5.31) * mm, "end": v(-6.13, 5.1) * mm});
            skLineSegment(sketch, "E339", {"start": v(-6.13, 5.1) * mm, "end": v(-6.44, 4.67) * mm});
            skLineSegment(sketch, "E340", {"start": v(-6.44, 4.67) * mm, "end": v(-6.6, 4.44) * mm});
            skLineSegment(sketch, "E341", {"start": v(-6.6, 4.44) * mm, "end": v(-6.87, 4) * mm});
            skLineSegment(sketch, "E342", {"start": v(-6.87, 4) * mm, "end": v(-7.1, 3.56) * mm});
            skLineSegment(sketch, "E343", {"start": v(-7.1, 3.56) * mm, "end": v(-7.2, 3.33) * mm});
            skLineSegment(sketch, "E344", {"start": v(-7.2, 3.33) * mm, "end": v(-7.39, 2.89) * mm});
            skLineSegment(sketch, "E345", {"start": v(-7.39, 2.89) * mm, "end": v(-7.5, 2.67) * mm});
            skLineSegment(sketch, "E346", {"start": v(-7.5, 2.67) * mm, "end": v(-7.67, 2.22) * mm});
            skLineSegment(sketch, "E347", {"start": v(-7.67, 2.22) * mm, "end": v(-7.77, 1.78) * mm});
            skLineSegment(sketch, "E348", {"start": v(-7.77, 1.78) * mm, "end": v(-7.8, 1.56) * mm});
            skLineSegment(sketch, "E349", {"start": v(-7.8, 1.56) * mm, "end": v(-7.86, 1.11) * mm});
            skLineSegment(sketch, "E350", {"start": v(-7.86, 1.11) * mm, "end": v(-7.91, 0.89) * mm});
            skLineSegment(sketch, "E351", {"start": v(-7.91, 0.89) * mm, "end": v(-7.98, 0.44) * mm});
            skLineSegment(sketch, "E352", {"start": v(-7.98, 0.44) * mm, "end": v(-7.98, 0) * mm});
            skLineSegment(sketch, "E353", {"start": v(-7.98, 0) * mm, "end": v(-7.91, -0.44) * mm});
            skLineSegment(sketch, "E354", {"start": v(-7.91, -0.44) * mm, "end": v(-7.86, -0.67) * mm});
            skLineSegment(sketch, "E355", {"start": v(-7.86, -0.67) * mm, "end": v(-7.8, -1.11) * mm});
            skLineSegment(sketch, "E356", {"start": v(-7.8, -1.11) * mm, "end": v(-7.77, -1.33) * mm});
            skLineSegment(sketch, "E357", {"start": v(-7.77, -1.33) * mm, "end": v(-7.7, -1.78) * mm});
            skLineSegment(sketch, "E358", {"start": v(-7.7, -1.78) * mm, "end": v(-7.64, -2) * mm});
            skLineSegment(sketch, "E359", {"start": v(-7.64, -2) * mm, "end": v(-7.52, -2.44) * mm});
            skLineSegment(sketch, "E360", {"start": v(-7.52, -2.44) * mm, "end": v(-7.47, -2.67) * mm});
            skLineSegment(sketch, "E361", {"start": v(-7.47, -2.67) * mm, "end": v(-7.33, -3.11) * mm});
            skLineSegment(sketch, "E362", {"start": v(-7.33, -3.11) * mm, "end": v(-7.24, -3.33) * mm});
            skLineSegment(sketch, "E363", {"start": v(-7.24, -3.33) * mm, "end": v(-7.02, -3.78) * mm});
            skLineSegment(sketch, "E364", {"start": v(-7.02, -3.78) * mm, "end": v(-6.88, -4) * mm});
            skLineSegment(sketch, "E365", {"start": v(-6.88, -4) * mm, "end": v(-6.58, -4.44) * mm});
            skLineSegment(sketch, "E366", {"start": v(-6.58, -4.44) * mm, "end": v(-6.41, -4.67) * mm});
            skLineSegment(sketch, "E367", {"start": v(-6.41, -4.67) * mm, "end": v(-6.08, -5.11) * mm});
            skLineSegment(sketch, "E368", {"start": v(-6.08, -5.11) * mm, "end": v(-5.91, -5.33) * mm});
            skLineSegment(sketch, "E369", {"start": v(-5.91, -5.33) * mm, "end": v(-5.54, -5.77) * mm});
            skLineSegment(sketch, "E370", {"start": v(-5.54, -5.77) * mm, "end": v(-5.33, -5.98) * mm});
            skLineSegment(sketch, "E371", {"start": v(-5.33, -5.98) * mm, "end": v(-4.89, -6.34) * mm});
            skLineSegment(sketch, "E372", {"start": v(-4.89, -6.34) * mm, "end": v(-4.44, -6.62) * mm});
            skLineSegment(sketch, "E373", {"start": v(-4.44, -6.62) * mm, "end": v(-4.22, -6.75) * mm});
            skLineSegment(sketch, "E374", {"start": v(-4.22, -6.75) * mm, "end": v(-4, -6.89) * mm});
            skLineSegment(sketch, "E375", {"start": v(-4, -6.89) * mm, "end": v(-3.56, -7.14) * mm});
            skLineSegment(sketch, "E376", {"start": v(-3.56, -7.14) * mm, "end": v(-3.11, -7.33) * mm});
            skLineSegment(sketch, "E377", {"start": v(-3.11, -7.33) * mm, "end": v(-2.89, -7.42) * mm});
            skLineSegment(sketch, "E378", {"start": v(-2.89, -7.42) * mm, "end": v(-2.44, -7.6) * mm});
            skLineSegment(sketch, "E379", {"start": v(-2.44, -7.6) * mm, "end": v(-2.22, -7.67) * mm});
            skLineSegment(sketch, "E380", {"start": v(-2.22, -7.67) * mm, "end": v(-1.78, -7.77) * mm});
            skLineSegment(sketch, "E381", {"start": v(-1.78, -7.77) * mm, "end": v(-1.56, -7.8) * mm});
            skLineSegment(sketch, "E382", {"start": v(-1.56, -7.8) * mm, "end": v(-1.11, -7.86) * mm});
            skLineSegment(sketch, "E383", {"start": v(-1.11, -7.86) * mm, "end": v(-0.89, -7.91) * mm});
            skLineSegment(sketch, "E384", {"start": v(-0.89, -7.91) * mm, "end": v(-0.44, -7.98) * mm});
            skLineSegment(sketch, "E385", {"start": v(-0.44, -7.98) * mm, "end": v(0, -7.98) * mm});
            skLineSegment(sketch, "E386", {"start": v(0, -7.98) * mm, "end": v(0.22, -7.95) * mm});
            skLineSegment(sketch, "E387", {"start": v(0.22, -7.95) * mm, "end": v(0.44, -7.91) * mm});
            skLineSegment(sketch, "E388", {"start": v(0.44, -7.91) * mm, "end": v(0.89, -7.83) * mm});
            skLineSegment(sketch, "E389", {"start": v(0.89, -7.83) * mm, "end": v(1.11, -7.8) * mm});
            skLineSegment(sketch, "E390", {"start": v(1.11, -7.8) * mm, "end": v(1.56, -7.76) * mm});
            skLineSegment(sketch, "E391", {"start": v(1.56, -7.76) * mm, "end": v(2, -7.67) * mm});
            skLineSegment(sketch, "E392", {"start": v(2, -7.67) * mm, "end": v(2.22, -7.6) * mm});
            skLineSegment(sketch, "E393", {"start": v(2.22, -7.6) * mm, "end": v(2.44, -7.51) * mm});
            skLineSegment(sketch, "E394", {"start": v(2.44, -7.51) * mm, "end": v(2.89, -7.33) * mm});
            skLineSegment(sketch, "E395", {"start": v(2.89, -7.33) * mm, "end": v(3.33, -7.15) * mm});
            skLineSegment(sketch, "E396", {"start": v(3.33, -7.15) * mm, "end": v(3.56, -7.06) * mm});
            skLineSegment(sketch, "E397", {"start": v(3.56, -7.06) * mm, "end": v(4, -6.84) * mm});
            skLineSegment(sketch, "E398", {"start": v(4, -6.84) * mm, "end": v(4.22, -6.72) * mm});
            skLineSegment(sketch, "E399", {"start": v(4.22, -6.72) * mm, "end": v(4.43, -6.61) * mm});
            skLineSegment(sketch, "E400", {"start": v(4.43, -6.61) * mm, "end": v(4.8, -6.36) * mm});
            skLineSegment(sketch, "E401", {"start": v(4.8, -6.36) * mm, "end": v(4.98, -6.22) * mm});
            skLineSegment(sketch, "E402", {"start": v(4.98, -6.22) * mm, "end": v(5.16, -6.07) * mm});
            skLineSegment(sketch, "E403", {"start": v(5.16, -6.07) * mm, "end": v(5.54, -5.73) * mm});
            skLineSegment(sketch, "E404", {"start": v(5.54, -5.73) * mm, "end": v(5.73, -5.54) * mm});
            skLineSegment(sketch, "E405", {"start": v(5.73, -5.54) * mm, "end": v(5.9, -5.35) * mm});
            skLineSegment(sketch, "E406", {"start": v(5.9, -5.35) * mm, "end": v(6.22, -4.98) * mm});
            skLineSegment(sketch, "E407", {"start": v(6.22, -4.98) * mm, "end": v(6.36, -4.8) * mm});
            skLineSegment(sketch, "E408", {"start": v(6.36, -4.8) * mm, "end": v(6.61, -4.43) * mm});
            skLineSegment(sketch, "E409", {"start": v(6.61, -4.43) * mm, "end": v(6.72, -4.22) * mm});
            skLineSegment(sketch, "E410", {"start": v(6.72, -4.22) * mm, "end": v(6.84, -4) * mm});
            skLineSegment(sketch, "E411", {"start": v(6.84, -4) * mm, "end": v(7.06, -3.56) * mm});
            skLineSegment(sketch, "E412", {"start": v(7.06, -3.56) * mm, "end": v(7.15, -3.33) * mm});
            skLineSegment(sketch, "E413", {"start": v(7.15, -3.33) * mm, "end": v(7.33, -2.89) * mm});
            skLineSegment(sketch, "E414", {"start": v(7.33, -2.89) * mm, "end": v(7.51, -2.44) * mm});
            skLineSegment(sketch, "E415", {"start": v(7.51, -2.44) * mm, "end": v(7.6, -2.22) * mm});
            skLineSegment(sketch, "E416", {"start": v(7.6, -2.22) * mm, "end": v(7.67, -2) * mm});
            skLineSegment(sketch, "E417", {"start": v(7.67, -2) * mm, "end": v(7.76, -1.56) * mm});
            skLineSegment(sketch, "E418", {"start": v(7.76, -1.56) * mm, "end": v(7.8, -1.11) * mm});
            skLineSegment(sketch, "E419", {"start": v(7.8, -1.11) * mm, "end": v(7.83, -0.89) * mm});
            skLineSegment(sketch, "E420", {"start": v(7.83, -0.89) * mm, "end": v(7.91, -0.44) * mm});
            skLineSegment(sketch, "E421", {"start": v(7.91, -0.44) * mm, "end": v(7.98, 0) * mm});
            skLineSegment(sketch, "E422", {"start": v(7.98, 0) * mm, "end": v(7.98, 0.44) * mm});
            skLineSegment(sketch, "E423", {"start": v(7.98, 0.44) * mm, "end": v(7.91, 0.89) * mm});
            skLineSegment(sketch, "E424", {"start": v(7.91, 0.89) * mm, "end": v(7.86, 1.11) * mm});
            skLineSegment(sketch, "E425", {"start": v(7.86, 1.11) * mm, "end": v(7.8, 1.56) * mm});
            skLineSegment(sketch, "E426", {"start": v(7.8, 1.56) * mm, "end": v(7.77, 1.78) * mm});
            skLineSegment(sketch, "E427", {"start": v(7.77, 1.78) * mm, "end": v(7.67, 2.22) * mm});
            skLineSegment(sketch, "E428", {"start": v(7.67, 2.22) * mm, "end": v(7.5, 2.67) * mm});
            skLineSegment(sketch, "E429", {"start": v(7.5, 2.67) * mm, "end": v(7.39, 2.89) * mm});
            skLineSegment(sketch, "E430", {"start": v(7.39, 2.89) * mm, "end": v(7.2, 3.33) * mm});
            skLineSegment(sketch, "E431", {"start": v(7.2, 3.33) * mm, "end": v(7.1, 3.56) * mm});
            skLineSegment(sketch, "E432", {"start": v(7.1, 3.56) * mm, "end": v(6.87, 4) * mm});
            skLineSegment(sketch, "E433", {"start": v(6.87, 4) * mm, "end": v(6.6, 4.44) * mm});
            skLineSegment(sketch, "E434", {"start": v(6.6, 4.44) * mm, "end": v(6.44, 4.67) * mm});
            skLineSegment(sketch, "E435", {"start": v(6.44, 4.67) * mm, "end": v(6.3, 4.89) * mm});
            skLineSegment(sketch, "E436", {"start": v(6.3, 4.89) * mm, "end": v(5.95, 5.33) * mm});
            skLineSegment(sketch, "E437", {"start": v(5.95, 5.33) * mm, "end": v(5.76, 5.54) * mm});
            skLineSegment(sketch, "E438", {"start": v(5.76, 5.54) * mm, "end": v(5.33, 5.91) * mm});
            skLineSegment(sketch, "E439", {"start": v(5.33, 5.91) * mm, "end": v(5.11, 6.08) * mm});
            skLineSegment(sketch, "E440", {"start": v(5.11, 6.08) * mm, "end": v(4.67, 6.4) * mm});
            skLineSegment(sketch, "E441", {"start": v(4.67, 6.4) * mm, "end": v(4.44, 6.57) * mm});
            skLineSegment(sketch, "E442", {"start": v(4.44, 6.57) * mm, "end": v(4, 6.83) * mm});
            skLineSegment(sketch, "E443", {"start": v(4, 6.83) * mm, "end": v(3.78, 6.94) * mm});
            skLineSegment(sketch, "E444", {"start": v(3.78, 6.94) * mm, "end": v(3.56, 7.06) * mm});
            skLineSegment(sketch, "E445", {"start": v(3.56, 7.06) * mm, "end": v(3.33, 7.16) * mm});
            skLineSegment(sketch, "E446", {"start": v(3.33, 7.16) * mm, "end": v(3.11, 7.28) * mm});
            skLineSegment(sketch, "E447", {"start": v(3.11, 7.28) * mm, "end": v(2.67, 7.46) * mm});
            skLineSegment(sketch, "E448", {"start": v(2.67, 7.46) * mm, "end": v(2.22, 7.59) * mm});
            skLineSegment(sketch, "E449", {"start": v(2.22, 7.59) * mm, "end": v(2, 7.64) * mm});
            skLineSegment(sketch, "E450", {"start": v(2, 7.64) * mm, "end": v(1.78, 7.7) * mm});
            skLineSegment(sketch, "E451", {"start": v(1.78, 7.7) * mm, "end": v(1.33, 7.76) * mm});
            skLineSegment(sketch, "E452", {"start": v(1.33, 7.76) * mm, "end": v(1.11, 7.77) * mm});
            skLineSegment(sketch, "E453", {"start": v(1.11, 7.77) * mm, "end": v(0.67, 7.78) * mm});
            skLineSegment(sketch, "E454", {"start": v(0.67, 7.78) * mm, "end": v(0.22, 7.78) * mm});
            skLineSegment(sketch, "E455", {"start": v(0.22, 7.78) * mm, "end": v(-0.67, 7.78) * mm});
            skLineSegment(sketch, "E456", {"start": v(-0.67, 7.78) * mm, "end": v(-1.11, 7.78) * mm});
            skLineSegment(sketch, "E457", {"start": v(-1.11, 7.78) * mm, "end": v(-1.33, 7.78) * mm});
            skLineSegment(sketch, "E458", {"start": v(-1.33, 7.78) * mm, "end": v(-1.78, 7.76) * mm});
            skLineSegment(sketch, "E459", {"start": v(-1.78, 7.76) * mm, "end": v(-2.22, 7.67) * mm});
            skLineSegment(sketch, "E460", {"start": v(-20, 0.44) * mm, "end": v(-20, -0.67) * mm});
            skLineSegment(sketch, "E461", {"start": v(-20, -0.67) * mm, "end": v(-12.44, -0.67) * mm});
            skLineSegment(sketch, "E462", {"start": v(-12.44, -0.67) * mm, "end": v(-12.44, 0.44) * mm});
            skLineSegment(sketch, "E463", {"start": v(-12.44, 0.44) * mm, "end": v(-20, 0.44) * mm});
            skLineSegment(sketch, "E464", {"start": v(-11.33, 0.44) * mm, "end": v(-11.33, -0.67) * mm});
            skLineSegment(sketch, "E465", {"start": v(-11.33, -0.67) * mm, "end": v(-9.11, -0.67) * mm});
            skLineSegment(sketch, "E466", {"start": v(-9.11, -0.67) * mm, "end": v(-9.11, 0.44) * mm});
            skLineSegment(sketch, "E467", {"start": v(-9.11, 0.44) * mm, "end": v(-11.33, 0.44) * mm});
            skLineSegment(sketch, "E468", {"start": v(9.11, 0.44) * mm, "end": v(9.11, -0.67) * mm});
            skLineSegment(sketch, "E469", {"start": v(9.11, -0.67) * mm, "end": v(11.33, -0.67) * mm});
            skLineSegment(sketch, "E470", {"start": v(11.33, -0.67) * mm, "end": v(11.33, 0.44) * mm});
            skLineSegment(sketch, "E471", {"start": v(11.33, 0.44) * mm, "end": v(9.11, 0.44) * mm});
            skLineSegment(sketch, "E472", {"start": v(12.44, 0.44) * mm, "end": v(12.44, -0.67) * mm});
            skLineSegment(sketch, "E473", {"start": v(12.44, -0.67) * mm, "end": v(20, -0.67) * mm});
            skLineSegment(sketch, "E474", {"start": v(20, -0.67) * mm, "end": v(20, 0.44) * mm});
            skLineSegment(sketch, "E475", {"start": v(20, 0.44) * mm, "end": v(12.44, 0.44) * mm});
            skLineSegment(sketch, "E476", {"start": v(-15.11, -2) * mm, "end": v(-14.94, -2.22) * mm});
            skLineSegment(sketch, "E477", {"start": v(-14.94, -2.22) * mm, "end": v(-14.82, -2.27) * mm});
            skLineSegment(sketch, "E478", {"start": v(-14.82, -2.27) * mm, "end": v(-14.44, -2.5) * mm});
            skLineSegment(sketch, "E479", {"start": v(-14.44, -2.5) * mm, "end": v(-14, -2.77) * mm});
            skLineSegment(sketch, "E480", {"start": v(-14, -2.77) * mm, "end": v(-13.56, -3.07) * mm});
            skLineSegment(sketch, "E481", {"start": v(-13.56, -3.07) * mm, "end": v(-13.33, -3.23) * mm});
            skLineSegment(sketch, "E482", {"start": v(-13.33, -3.23) * mm, "end": v(-12.89, -3.52) * mm});
            skLineSegment(sketch, "E483", {"start": v(-12.89, -3.52) * mm, "end": v(-12.67, -3.65) * mm});
            skLineSegment(sketch, "E484", {"start": v(-12.67, -3.65) * mm, "end": v(-12.22, -3.96) * mm});
            skLineSegment(sketch, "E485", {"start": v(-12.22, -3.96) * mm, "end": v(-12, -4.12) * mm});
            skLineSegment(sketch, "E486", {"start": v(-12, -4.12) * mm, "end": v(-11.8, -4.23) * mm});
            skLineSegment(sketch, "E487", {"start": v(-11.8, -4.23) * mm, "end": v(-11.44, -4.38) * mm});
            skLineSegment(sketch, "E488", {"start": v(-11.44, -4.38) * mm, "end": v(-11.11, -4.44) * mm});
            skLineSegment(sketch, "E489", {"start": v(-11.11, -4.44) * mm, "end": v(-11.11, -4.9) * mm});
            skLineSegment(sketch, "E490", {"start": v(-11.11, -4.9) * mm, "end": v(-11.12, -5.33) * mm});
            skLineSegment(sketch, "E491", {"start": v(-11.12, -5.33) * mm, "end": v(-11.13, -5.56) * mm});
            skLineSegment(sketch, "E492", {"start": v(-11.13, -5.56) * mm, "end": v(-11.2, -6) * mm});
            skLineSegment(sketch, "E493", {"start": v(-11.2, -6) * mm, "end": v(-11.25, -6.22) * mm});
            skLineSegment(sketch, "E494", {"start": v(-11.25, -6.22) * mm, "end": v(-11.3, -6.44) * mm});
            skLineSegment(sketch, "E495", {"start": v(-11.3, -6.44) * mm, "end": v(-11.36, -6.67) * mm});
            skLineSegment(sketch, "E496", {"start": v(-11.36, -6.67) * mm, "end": v(-11.47, -7.11) * mm});
            skLineSegment(sketch, "E497", {"start": v(-11.47, -7.11) * mm, "end": v(-11.51, -7.33) * mm});
            skLineSegment(sketch, "E498", {"start": v(-11.51, -7.33) * mm, "end": v(-11.62, -7.78) * mm});
            skLineSegment(sketch, "E499", {"start": v(-11.62, -7.78) * mm, "end": v(-11.78, -8.22) * mm});
            skLineSegment(sketch, "E500", {"start": v(-11.78, -8.22) * mm, "end": v(-11.87, -8.44) * mm});
            skLineSegment(sketch, "E501", {"start": v(-11.87, -8.44) * mm, "end": v(-12.02, -8.89) * mm});
            skLineSegment(sketch, "E502", {"start": v(-12.02, -8.89) * mm, "end": v(-12.08, -9.1) * mm});
            skLineSegment(sketch, "E503", {"start": v(-12.08, -9.1) * mm, "end": v(-12.17, -9.44) * mm});
            skLineSegment(sketch, "E504", {"start": v(-12.17, -9.44) * mm, "end": v(-12.22, -9.78) * mm});
            skLineSegment(sketch, "E505", {"start": v(-12.22, -9.78) * mm, "end": v(-11.9, -9.66) * mm});
            skLineSegment(sketch, "E506", {"start": v(-11.9, -9.66) * mm, "end": v(-11.6, -9.44) * mm});
            skLineSegment(sketch, "E507", {"start": v(-11.6, -9.44) * mm, "end": v(-11.42, -9.28) * mm});
            skLineSegment(sketch, "E508", {"start": v(-11.42, -9.28) * mm, "end": v(-11.25, -9.1) * mm});
            skLineSegment(sketch, "E509", {"start": v(-11.25, -9.1) * mm, "end": v(-10.87, -8.67) * mm});
            skLineSegment(sketch, "E510", {"start": v(-10.87, -8.67) * mm, "end": v(-10.66, -8.44) * mm});
            skLineSegment(sketch, "E511", {"start": v(-10.66, -8.44) * mm, "end": v(-10.22, -8) * mm});
            skLineSegment(sketch, "E512", {"start": v(-10.22, -8) * mm, "end": v(-10, -7.78) * mm});
            skLineSegment(sketch, "E513", {"start": v(-10, -7.78) * mm, "end": v(-9.56, -7.33) * mm});
            skLineSegment(sketch, "E514", {"start": v(-9.56, -7.33) * mm, "end": v(-9.16, -6.9) * mm});
            skLineSegment(sketch, "E515", {"start": v(-9.16, -6.9) * mm, "end": v(-8.8, -6.5) * mm});
            skLineSegment(sketch, "E516", {"start": v(-8.8, -6.5) * mm, "end": v(-8.62, -6.3) * mm});
            skLineSegment(sketch, "E517", {"start": v(-8.62, -6.3) * mm, "end": v(-8.23, -5.98) * mm});
            skLineSegment(sketch, "E518", {"start": v(-8.23, -5.98) * mm, "end": v(-8.01, -5.83) * mm});
            skLineSegment(sketch, "E519", {"start": v(-8.01, -5.83) * mm, "end": v(-7.89, -5.72) * mm});
            skLineSegment(sketch, "E520", {"start": v(-7.89, -5.72) * mm, "end": v(-7.56, -5.56) * mm});
            skLineSegment(sketch, "E521", {"start": v(-7.56, -5.56) * mm, "end": v(-7.57, -5.22) * mm});
            skLineSegment(sketch, "E522", {"start": v(-7.57, -5.22) * mm, "end": v(-7.66, -4.88) * mm});
            skLineSegment(sketch, "E523", {"start": v(-7.66, -4.88) * mm, "end": v(-7.74, -4.67) * mm});
            skLineSegment(sketch, "E524", {"start": v(-7.74, -4.67) * mm, "end": v(-7.82, -4.44) * mm});
            skLineSegment(sketch, "E525", {"start": v(-7.82, -4.44) * mm, "end": v(-7.92, -4.22) * mm});
            skLineSegment(sketch, "E526", {"start": v(-7.92, -4.22) * mm, "end": v(-8.01, -4) * mm});
            skLineSegment(sketch, "E527", {"start": v(-8.01, -4) * mm, "end": v(-8.23, -3.56) * mm});
            skLineSegment(sketch, "E528", {"start": v(-8.23, -3.56) * mm, "end": v(-8.36, -3.33) * mm});
            skLineSegment(sketch, "E529", {"start": v(-8.36, -3.33) * mm, "end": v(-8.6, -2.89) * mm});
            skLineSegment(sketch, "E530", {"start": v(-8.6, -2.89) * mm, "end": v(-8.7, -2.68) * mm});
            skLineSegment(sketch, "E531", {"start": v(-8.7, -2.68) * mm, "end": v(-8.83, -2.33) * mm});
            skLineSegment(sketch, "E532", {"start": v(-8.83, -2.33) * mm, "end": v(-8.89, -2) * mm});
            skLineSegment(sketch, "E533", {"start": v(-8.89, -2) * mm, "end": v(-15.11, -2) * mm});
            skLineSegment(sketch, "E534", {"start": v(9.11, -2) * mm, "end": v(8.89, -2.33) * mm});
            skLineSegment(sketch, "E535", {"start": v(8.89, -2.33) * mm, "end": v(8.84, -2.46) * mm});
            skLineSegment(sketch, "E536", {"start": v(8.84, -2.46) * mm, "end": v(8.61, -2.89) * mm});
            skLineSegment(sketch, "E537", {"start": v(8.61, -2.89) * mm, "end": v(8.36, -3.33) * mm});
            skLineSegment(sketch, "E538", {"start": v(8.36, -3.33) * mm, "end": v(8.24, -3.56) * mm});
            skLineSegment(sketch, "E539", {"start": v(8.24, -3.56) * mm, "end": v(8.14, -3.78) * mm});
            skLineSegment(sketch, "E540", {"start": v(8.14, -3.78) * mm, "end": v(7.98, -4.22) * mm});
            skLineSegment(sketch, "E541", {"start": v(7.98, -4.22) * mm, "end": v(7.92, -4.44) * mm});
            skLineSegment(sketch, "E542", {"start": v(7.92, -4.44) * mm, "end": v(7.87, -4.67) * mm});
            skLineSegment(sketch, "E543", {"start": v(7.87, -4.67) * mm, "end": v(7.87, -5.11) * mm});
            skLineSegment(sketch, "E544", {"start": v(7.87, -5.11) * mm, "end": v(7.94, -5.33) * mm});
            skLineSegment(sketch, "E545", {"start": v(7.94, -5.33) * mm, "end": v(8.07, -5.56) * mm});
            skLineSegment(sketch, "E546", {"start": v(8.07, -5.56) * mm, "end": v(8.45, -6) * mm});
            skLineSegment(sketch, "E547", {"start": v(8.45, -6) * mm, "end": v(8.67, -6.22) * mm});
            skLineSegment(sketch, "E548", {"start": v(8.67, -6.22) * mm, "end": v(9.11, -6.67) * mm});
            skLineSegment(sketch, "E549", {"start": v(9.11, -6.67) * mm, "end": v(9.56, -7.11) * mm});
            skLineSegment(sketch, "E550", {"start": v(9.56, -7.11) * mm, "end": v(10.22, -7.78) * mm});
            skLineSegment(sketch, "E551", {"start": v(10.22, -7.78) * mm, "end": v(10.67, -8.22) * mm});
            skLineSegment(sketch, "E552", {"start": v(10.67, -8.22) * mm, "end": v(11.1, -8.66) * mm});
            skLineSegment(sketch, "E553", {"start": v(11.1, -8.66) * mm, "end": v(11.28, -8.87) * mm});
            skLineSegment(sketch, "E554", {"start": v(11.28, -8.87) * mm, "end": v(11.63, -9.22) * mm});
            skLineSegment(sketch, "E555", {"start": v(11.63, -9.22) * mm, "end": v(11.81, -9.35) * mm});
            skLineSegment(sketch, "E556", {"start": v(11.81, -9.35) * mm, "end": v(11.9, -9.44) * mm});
            skLineSegment(sketch, "E557", {"start": v(11.9, -9.44) * mm, "end": v(12.22, -9.56) * mm});
            skLineSegment(sketch, "E558", {"start": v(12.22, -9.56) * mm, "end": v(12.22, -9.22) * mm});
            skLineSegment(sketch, "E559", {"start": v(12.22, -9.22) * mm, "end": v(12.17, -8.88) * mm});
            skLineSegment(sketch, "E560", {"start": v(12.17, -8.88) * mm, "end": v(12.12, -8.67) * mm});
            skLineSegment(sketch, "E561", {"start": v(12.12, -8.67) * mm, "end": v(11.96, -8.22) * mm});
            skLineSegment(sketch, "E562", {"start": v(11.96, -8.22) * mm, "end": v(11.78, -7.78) * mm});
            skLineSegment(sketch, "E563", {"start": v(11.78, -7.78) * mm, "end": v(11.64, -7.33) * mm});
            skLineSegment(sketch, "E564", {"start": v(11.64, -7.33) * mm, "end": v(11.59, -7.11) * mm});
            skLineSegment(sketch, "E565", {"start": v(11.59, -7.11) * mm, "end": v(11.48, -6.67) * mm});
            skLineSegment(sketch, "E566", {"start": v(11.48, -6.67) * mm, "end": v(11.42, -6.44) * mm});
            skLineSegment(sketch, "E567", {"start": v(11.42, -6.44) * mm, "end": v(11.38, -6.22) * mm});
            skLineSegment(sketch, "E568", {"start": v(11.38, -6.22) * mm, "end": v(11.32, -5.78) * mm});
            skLineSegment(sketch, "E569", {"start": v(11.32, -5.78) * mm, "end": v(11.27, -5.33) * mm});
            skLineSegment(sketch, "E570", {"start": v(11.27, -5.33) * mm, "end": v(11.32, -4.89) * mm});
            skLineSegment(sketch, "E571", {"start": v(11.32, -4.89) * mm, "end": v(11.59, -4.45) * mm});
            skLineSegment(sketch, "E572", {"start": v(11.59, -4.45) * mm, "end": v(11.78, -4.24) * mm});
            skLineSegment(sketch, "E573", {"start": v(11.78, -4.24) * mm, "end": v(12, -4.06) * mm});
            skLineSegment(sketch, "E574", {"start": v(12, -4.06) * mm, "end": v(12.22, -3.88) * mm});
            skLineSegment(sketch, "E575", {"start": v(12.22, -3.88) * mm, "end": v(12.44, -3.74) * mm});
            skLineSegment(sketch, "E576", {"start": v(12.44, -3.74) * mm, "end": v(12.89, -3.46) * mm});
            skLineSegment(sketch, "E577", {"start": v(12.89, -3.46) * mm, "end": v(13.33, -3.15) * mm});
            skLineSegment(sketch, "E578", {"start": v(13.33, -3.15) * mm, "end": v(13.56, -2.99) * mm});
            skLineSegment(sketch, "E579", {"start": v(13.56, -2.99) * mm, "end": v(14, -2.72) * mm});
            skLineSegment(sketch, "E580", {"start": v(14, -2.72) * mm, "end": v(14.2, -2.62) * mm});
            skLineSegment(sketch, "E581", {"start": v(14.2, -2.62) * mm, "end": v(14.43, -2.5) * mm});
            skLineSegment(sketch, "E582", {"start": v(14.43, -2.5) * mm, "end": v(14.56, -2.44) * mm});
            skLineSegment(sketch, "E583", {"start": v(14.56, -2.44) * mm, "end": v(14.89, -2.22) * mm});
            skLineSegment(sketch, "E584", {"start": v(14.89, -2.22) * mm, "end": v(14.72, -2.06) * mm});
            skLineSegment(sketch, "E585", {"start": v(14.72, -2.06) * mm, "end": v(14.6, -2.06) * mm});
            skLineSegment(sketch, "E586", {"start": v(14.6, -2.06) * mm, "end": v(14.42, -2.01) * mm});
            skLineSegment(sketch, "E587", {"start": v(14.42, -2.01) * mm, "end": v(14.22, -2) * mm});
            skLineSegment(sketch, "E588", {"start": v(14.22, -2) * mm, "end": v(13.78, -2) * mm});
            skLineSegment(sketch, "E589", {"start": v(13.78, -2) * mm, "end": v(13.56, -2) * mm});
            skLineSegment(sketch, "E590", {"start": v(13.56, -2) * mm, "end": v(12.89, -2) * mm});
            skLineSegment(sketch, "E591", {"start": v(12.89, -2) * mm, "end": v(9.11, -2) * mm});
            skLineSegment(sketch, "E592", {"start": v(6.67, -6.22) * mm, "end": v(6.41, -6.56) * mm});
            skLineSegment(sketch, "E593", {"start": v(6.41, -6.56) * mm, "end": v(6.37, -6.67) * mm});
            skLineSegment(sketch, "E594", {"start": v(6.37, -6.67) * mm, "end": v(6.25, -7) * mm});
            skLineSegment(sketch, "E595", {"start": v(6.25, -7) * mm, "end": v(6.22, -7.33) * mm});
            skLineSegment(sketch, "E596", {"start": v(6.22, -7.33) * mm, "end": v(6.56, -7.5) * mm});
            skLineSegment(sketch, "E597", {"start": v(6.56, -7.5) * mm, "end": v(6.68, -7.62) * mm});
            skLineSegment(sketch, "E598", {"start": v(6.68, -7.62) * mm, "end": v(6.9, -7.78) * mm});
            skLineSegment(sketch, "E599", {"start": v(6.9, -7.78) * mm, "end": v(7.32, -8.06) * mm});
            skLineSegment(sketch, "E600", {"start": v(7.32, -8.06) * mm, "end": v(7.67, -8.2) * mm});
            skLineSegment(sketch, "E601", {"start": v(7.67, -8.2) * mm, "end": v(8, -8.22) * mm});
            skLineSegment(sketch, "E602", {"start": v(8, -8.22) * mm, "end": v(8.22, -8) * mm});
            skLineSegment(sketch, "E603", {"start": v(8.22, -8) * mm, "end": v(8.22, -7.33) * mm});
            skLineSegment(sketch, "E604", {"start": v(8.22, -7.33) * mm, "end": v(7.9, -7.1) * mm});
            skLineSegment(sketch, "E605", {"start": v(7.9, -7.1) * mm, "end": v(7.64, -6.88) * mm});
            skLineSegment(sketch, "E606", {"start": v(7.64, -6.88) * mm, "end": v(7.5, -6.75) * mm});
            skLineSegment(sketch, "E607", {"start": v(7.5, -6.75) * mm, "end": v(7.35, -6.59) * mm});
            skLineSegment(sketch, "E608", {"start": v(7.35, -6.59) * mm, "end": v(7.27, -6.5) * mm});
            skLineSegment(sketch, "E609", {"start": v(7.27, -6.5) * mm, "end": v(7.11, -6.22) * mm});
            skLineSegment(sketch, "E610", {"start": v(7.11, -6.22) * mm, "end": v(6.67, -6.22) * mm});
            skLineSegment(sketch, "E611", {"start": v(-7.78, -8.22) * mm, "end": v(-7.44, -8.2) * mm});
            skLineSegment(sketch, "E612", {"start": v(-7.44, -8.2) * mm, "end": v(-7.1, -8.06) * mm});
            skLineSegment(sketch, "E613", {"start": v(-7.1, -8.06) * mm, "end": v(-6.68, -7.78) * mm});
            skLineSegment(sketch, "E614", {"start": v(-6.68, -7.78) * mm, "end": v(-6.46, -7.62) * mm});
            skLineSegment(sketch, "E615", {"start": v(-6.46, -7.62) * mm, "end": v(-6.33, -7.5) * mm});
            skLineSegment(sketch, "E616", {"start": v(-6.33, -7.5) * mm, "end": v(-6, -7.33) * mm});
            skLineSegment(sketch, "E617", {"start": v(-6, -7.33) * mm, "end": v(-6, -6.67) * mm});
            skLineSegment(sketch, "E618", {"start": v(-6, -6.67) * mm, "end": v(-6.46, -6.54) * mm});
            skLineSegment(sketch, "E619", {"start": v(-6.46, -6.54) * mm, "end": v(-6.68, -6.52) * mm});
            skLineSegment(sketch, "E620", {"start": v(-6.68, -6.52) * mm, "end": v(-6.88, -6.54) * mm});
            skLineSegment(sketch, "E621", {"start": v(-6.88, -6.54) * mm, "end": v(-7.28, -6.74) * mm});
            skLineSegment(sketch, "E622", {"start": v(-7.28, -6.74) * mm, "end": v(-7.57, -7.12) * mm});
            skLineSegment(sketch, "E623", {"start": v(-7.57, -7.12) * mm, "end": v(-7.67, -7.33) * mm});
            skLineSegment(sketch, "E624", {"start": v(-7.67, -7.33) * mm, "end": v(-7.72, -7.54) * mm});
            skLineSegment(sketch, "E625", {"start": v(-7.72, -7.54) * mm, "end": v(-7.77, -7.89) * mm});
            skLineSegment(sketch, "E626", {"start": v(-7.77, -7.89) * mm, "end": v(-7.78, -8.22) * mm});
            skLineSegment(sketch, "E627", {"start": v(-5.11, -7.78) * mm, "end": v(-5.28, -8.1) * mm});
            skLineSegment(sketch, "E628", {"start": v(-5.28, -8.1) * mm, "end": v(-5.4, -8.18) * mm});
            skLineSegment(sketch, "E629", {"start": v(-5.4, -8.18) * mm, "end": v(-5.57, -8.35) * mm});
            skLineSegment(sketch, "E630", {"start": v(-5.57, -8.35) * mm, "end": v(-5.77, -8.48) * mm});
            skLineSegment(sketch, "E631", {"start": v(-5.77, -8.48) * mm, "end": v(-6.14, -8.77) * mm});
            skLineSegment(sketch, "E632", {"start": v(-6.14, -8.77) * mm, "end": v(-6.3, -8.94) * mm});
            skLineSegment(sketch, "E633", {"start": v(-6.3, -8.94) * mm, "end": v(-6.69, -9.34) * mm});
            skLineSegment(sketch, "E634", {"start": v(-6.69, -9.34) * mm, "end": v(-7.1, -9.78) * mm});
            skLineSegment(sketch, "E635", {"start": v(-7.1, -9.78) * mm, "end": v(-7.47, -10.2) * mm});
            skLineSegment(sketch, "E636", {"start": v(-7.47, -10.2) * mm, "end": v(-7.64, -10.4) * mm});
            skLineSegment(sketch, "E637", {"start": v(-7.64, -10.4) * mm, "end": v(-7.83, -10.58) * mm});
            skLineSegment(sketch, "E638", {"start": v(-7.83, -10.58) * mm, "end": v(-8.22, -10.94) * mm});
            skLineSegment(sketch, "E639", {"start": v(-8.22, -10.94) * mm, "end": v(-8.42, -11.13) * mm});
            skLineSegment(sketch, "E640", {"start": v(-8.42, -11.13) * mm, "end": v(-8.6, -11.33) * mm});
            skLineSegment(sketch, "E641", {"start": v(-8.6, -11.33) * mm, "end": v(-8.8, -11.67) * mm});
            skLineSegment(sketch, "E642", {"start": v(-8.8, -11.67) * mm, "end": v(-8.89, -12) * mm});
            skLineSegment(sketch, "E643", {"start": v(-8.89, -12) * mm, "end": v(-8.43, -12) * mm});
            skLineSegment(sketch, "E644", {"start": v(-8.43, -12) * mm, "end": v(-8, -11.94) * mm});
            skLineSegment(sketch, "E645", {"start": v(-8, -11.94) * mm, "end": v(-7.78, -11.9) * mm});
            skLineSegment(sketch, "E646", {"start": v(-7.78, -11.9) * mm, "end": v(-7.33, -11.74) * mm});
            skLineSegment(sketch, "E647", {"start": v(-7.33, -11.74) * mm, "end": v(-7.11, -11.65) * mm});
            skLineSegment(sketch, "E648", {"start": v(-7.11, -11.65) * mm, "end": v(-6.67, -11.52) * mm});
            skLineSegment(sketch, "E649", {"start": v(-6.67, -11.52) * mm, "end": v(-6.44, -11.47) * mm});
            skLineSegment(sketch, "E650", {"start": v(-6.44, -11.47) * mm, "end": v(-6, -11.33) * mm});
            skLineSegment(sketch, "E651", {"start": v(-6, -11.33) * mm, "end": v(-5.78, -11.27) * mm});
            skLineSegment(sketch, "E652", {"start": v(-5.78, -11.27) * mm, "end": v(-5.33, -11.17) * mm});
            skLineSegment(sketch, "E653", {"start": v(-5.33, -11.17) * mm, "end": v(-5.11, -11.15) * mm});
            skLineSegment(sketch, "E654", {"start": v(-5.11, -11.15) * mm, "end": v(-4.67, -11.27) * mm});
            skLineSegment(sketch, "E655", {"start": v(-4.67, -11.27) * mm, "end": v(-4.46, -11.4) * mm});
            skLineSegment(sketch, "E656", {"start": v(-4.46, -11.4) * mm, "end": v(-4.27, -11.58) * mm});
            skLineSegment(sketch, "E657", {"start": v(-4.27, -11.58) * mm, "end": v(-4.09, -11.78) * mm});
            skLineSegment(sketch, "E658", {"start": v(-4.09, -11.78) * mm, "end": v(-3.75, -12.22) * mm});
            skLineSegment(sketch, "E659", {"start": v(-3.75, -12.22) * mm, "end": v(-3.43, -12.67) * mm});
            skLineSegment(sketch, "E660", {"start": v(-3.43, -12.67) * mm, "end": v(-3.3, -12.89) * mm});
            skLineSegment(sketch, "E661", {"start": v(-3.3, -12.89) * mm, "end": v(-3.01, -13.33) * mm});
            skLineSegment(sketch, "E662", {"start": v(-3.01, -13.33) * mm, "end": v(-2.86, -13.56) * mm});
            skLineSegment(sketch, "E663", {"start": v(-2.86, -13.56) * mm, "end": v(-2.58, -14) * mm});
            skLineSegment(sketch, "E664", {"start": v(-2.58, -14) * mm, "end": v(-2.38, -14.44) * mm});
            skLineSegment(sketch, "E665", {"start": v(-2.38, -14.44) * mm, "end": v(-2.3, -14.65) * mm});
            skLineSegment(sketch, "E666", {"start": v(-2.3, -14.65) * mm, "end": v(-2.22, -14.88) * mm});
            skLineSegment(sketch, "E667", {"start": v(-2.22, -14.88) * mm, "end": v(-2.18, -15) * mm});
            skLineSegment(sketch, "E668", {"start": v(-2.18, -15) * mm, "end": v(-2, -15.33) * mm});
            skLineSegment(sketch, "E669", {"start": v(-2, -15.33) * mm, "end": v(-1.84, -15.16) * mm});
            skLineSegment(sketch, "E670", {"start": v(-1.84, -15.16) * mm, "end": v(-1.83, -15.04) * mm});
            skLineSegment(sketch, "E671", {"start": v(-1.83, -15.04) * mm, "end": v(-1.8, -14.86) * mm});
            skLineSegment(sketch, "E672", {"start": v(-1.8, -14.86) * mm, "end": v(-1.78, -14.66) * mm});
            skLineSegment(sketch, "E673", {"start": v(-1.78, -14.66) * mm, "end": v(-1.78, -14.22) * mm});
            skLineSegment(sketch, "E674", {"start": v(-1.78, -14.22) * mm, "end": v(-1.78, -14) * mm});
            skLineSegment(sketch, "E675", {"start": v(-1.78, -14) * mm, "end": v(-1.78, -13.33) * mm});
            skLineSegment(sketch, "E676", {"start": v(-1.78, -13.33) * mm, "end": v(-1.78, -8.89) * mm});
            skLineSegment(sketch, "E677", {"start": v(-1.78, -8.89) * mm, "end": v(-2.23, -8.75) * mm});
            skLineSegment(sketch, "E678", {"start": v(-2.23, -8.75) * mm, "end": v(-2.67, -8.64) * mm});
            skLineSegment(sketch, "E679", {"start": v(-2.67, -8.64) * mm, "end": v(-2.89, -8.58) * mm});
            skLineSegment(sketch, "E680", {"start": v(-2.89, -8.58) * mm, "end": v(-3.33, -8.43) * mm});
            skLineSegment(sketch, "E681", {"start": v(-3.33, -8.43) * mm, "end": v(-3.78, -8.2) * mm});
            skLineSegment(sketch, "E682", {"start": v(-3.78, -8.2) * mm, "end": v(-4, -8.09) * mm});
            skLineSegment(sketch, "E683", {"start": v(-4, -8.09) * mm, "end": v(-4.43, -7.89) * mm});
            skLineSegment(sketch, "E684", {"start": v(-4.43, -7.89) * mm, "end": v(-4.78, -7.8) * mm});
            skLineSegment(sketch, "E685", {"start": v(-4.78, -7.8) * mm, "end": v(-5.11, -7.78) * mm});
            skLineSegment(sketch, "E686", {"start": v(4.67, -7.78) * mm, "end": v(4.33, -8.05) * mm});
            skLineSegment(sketch, "E687", {"start": v(4.33, -8.05) * mm, "end": v(3.99, -8.25) * mm});
            skLineSegment(sketch, "E688", {"start": v(3.99, -8.25) * mm, "end": v(3.78, -8.34) * mm});
            skLineSegment(sketch, "E689", {"start": v(3.78, -8.34) * mm, "end": v(3.33, -8.48) * mm});
            skLineSegment(sketch, "E690", {"start": v(3.33, -8.48) * mm, "end": v(2.89, -8.58) * mm});
            skLineSegment(sketch, "E691", {"start": v(2.89, -8.58) * mm, "end": v(2.46, -8.65) * mm});
            skLineSegment(sketch, "E692", {"start": v(2.46, -8.65) * mm, "end": v(2.33, -8.66) * mm});
            skLineSegment(sketch, "E693", {"start": v(2.33, -8.66) * mm, "end": v(2, -8.67) * mm});
            skLineSegment(sketch, "E694", {"start": v(2, -8.67) * mm, "end": v(1.78, -8.89) * mm});
            skLineSegment(sketch, "E695", {"start": v(1.78, -8.89) * mm, "end": v(1.78, -15.56) * mm});
            skLineSegment(sketch, "E696", {"start": v(1.78, -15.56) * mm, "end": v(2.05, -15.38) * mm});
            skLineSegment(sketch, "E697", {"start": v(2.05, -15.38) * mm, "end": v(2.13, -15.27) * mm});
            skLineSegment(sketch, "E698", {"start": v(2.13, -15.27) * mm, "end": v(2.38, -14.88) * mm});
            skLineSegment(sketch, "E699", {"start": v(2.38, -14.88) * mm, "end": v(2.58, -14.44) * mm});
            skLineSegment(sketch, "E700", {"start": v(2.58, -14.44) * mm, "end": v(2.76, -14) * mm});
            skLineSegment(sketch, "E701", {"start": v(2.76, -14) * mm, "end": v(3, -13.56) * mm});
            skLineSegment(sketch, "E702", {"start": v(3, -13.56) * mm, "end": v(3.3, -13.11) * mm});
            skLineSegment(sketch, "E703", {"start": v(3.3, -13.11) * mm, "end": v(3.46, -12.89) * mm});
            skLineSegment(sketch, "E704", {"start": v(3.46, -12.89) * mm, "end": v(3.74, -12.44) * mm});
            skLineSegment(sketch, "E705", {"start": v(3.74, -12.44) * mm, "end": v(3.88, -12.23) * mm});
            skLineSegment(sketch, "E706", {"start": v(3.88, -12.23) * mm, "end": v(4.24, -11.83) * mm});
            skLineSegment(sketch, "E707", {"start": v(4.24, -11.83) * mm, "end": v(4.45, -11.67) * mm});
            skLineSegment(sketch, "E708", {"start": v(4.45, -11.67) * mm, "end": v(4.67, -11.54) * mm});
            skLineSegment(sketch, "E709", {"start": v(4.67, -11.54) * mm, "end": v(4.89, -11.44) * mm});
            skLineSegment(sketch, "E710", {"start": v(4.89, -11.44) * mm, "end": v(5.33, -11.35) * mm});
            skLineSegment(sketch, "E711", {"start": v(5.33, -11.35) * mm, "end": v(5.78, -11.34) * mm});
            skLineSegment(sketch, "E712", {"start": v(5.78, -11.34) * mm, "end": v(6, -11.35) * mm});
            skLineSegment(sketch, "E713", {"start": v(6, -11.35) * mm, "end": v(6.44, -11.42) * mm});
            skLineSegment(sketch, "E714", {"start": v(6.44, -11.42) * mm, "end": v(6.67, -11.48) * mm});
            skLineSegment(sketch, "E715", {"start": v(6.67, -11.48) * mm, "end": v(7.11, -11.59) * mm});
            skLineSegment(sketch, "E716", {"start": v(7.11, -11.59) * mm, "end": v(7.33, -11.64) * mm});
            skLineSegment(sketch, "E717", {"start": v(7.33, -11.64) * mm, "end": v(7.78, -11.78) * mm});
            skLineSegment(sketch, "E718", {"start": v(7.78, -11.78) * mm, "end": v(8.22, -11.96) * mm});
            skLineSegment(sketch, "E719", {"start": v(8.22, -11.96) * mm, "end": v(8.67, -12.12) * mm});
            skLineSegment(sketch, "E720", {"start": v(8.67, -12.12) * mm, "end": v(8.88, -12.17) * mm});
            skLineSegment(sketch, "E721", {"start": v(8.88, -12.17) * mm, "end": v(9.22, -12.22) * mm});
            skLineSegment(sketch, "E722", {"start": v(9.22, -12.22) * mm, "end": v(9.56, -12.22) * mm});
            skLineSegment(sketch, "E723", {"start": v(9.56, -12.22) * mm, "end": v(9.44, -11.9) * mm});
            skLineSegment(sketch, "E724", {"start": v(9.44, -11.9) * mm, "end": v(9.35, -11.81) * mm});
            skLineSegment(sketch, "E725", {"start": v(9.35, -11.81) * mm, "end": v(9.22, -11.63) * mm});
            skLineSegment(sketch, "E726", {"start": v(9.22, -11.63) * mm, "end": v(8.87, -11.28) * mm});
            skLineSegment(sketch, "E727", {"start": v(8.87, -11.28) * mm, "end": v(8.66, -11.1) * mm});
            skLineSegment(sketch, "E728", {"start": v(8.66, -11.1) * mm, "end": v(8.22, -10.67) * mm});
            skLineSegment(sketch, "E729", {"start": v(8.22, -10.67) * mm, "end": v(8, -10.44) * mm});
            skLineSegment(sketch, "E730", {"start": v(8, -10.44) * mm, "end": v(7.56, -10.02) * mm});
            skLineSegment(sketch, "E731", {"start": v(7.56, -10.02) * mm, "end": v(7.34, -9.83) * mm});
            skLineSegment(sketch, "E732", {"start": v(7.34, -9.83) * mm, "end": v(6.94, -9.47) * mm});
            skLineSegment(sketch, "E733", {"start": v(6.94, -9.47) * mm, "end": v(6.75, -9.28) * mm});
            skLineSegment(sketch, "E734", {"start": v(6.75, -9.28) * mm, "end": v(6.4, -8.9) * mm});
            skLineSegment(sketch, "E735", {"start": v(6.4, -8.9) * mm, "end": v(6.2, -8.72) * mm});
            skLineSegment(sketch, "E736", {"start": v(6.2, -8.72) * mm, "end": v(5.8, -8.37) * mm});
            skLineSegment(sketch, "E737", {"start": v(5.8, -8.37) * mm, "end": v(5.57, -8.19) * mm});
            skLineSegment(sketch, "E738", {"start": v(5.57, -8.19) * mm, "end": v(5.44, -8.1) * mm});
            skLineSegment(sketch, "E739", {"start": v(5.44, -8.1) * mm, "end": v(5.11, -7.78) * mm});
            skLineSegment(sketch, "E740", {"start": v(5.11, -7.78) * mm, "end": v(4.67, -7.78) * mm});
            skLineSegment(sketch, "E741", {"start": v(-9.33, -8.67) * mm, "end": v(-9.5, -8.98) * mm});
            skLineSegment(sketch, "E742", {"start": v(-9.5, -8.98) * mm, "end": v(-9.62, -9.06) * mm});
            skLineSegment(sketch, "E743", {"start": v(-9.62, -9.06) * mm, "end": v(-9.8, -9.2) * mm});
            skLineSegment(sketch, "E744", {"start": v(-9.8, -9.2) * mm, "end": v(-9.99, -9.33) * mm});
            skLineSegment(sketch, "E745", {"start": v(-9.99, -9.33) * mm, "end": v(-10.36, -9.62) * mm});
            skLineSegment(sketch, "E746", {"start": v(-10.36, -9.62) * mm, "end": v(-10.7, -10) * mm});
            skLineSegment(sketch, "E747", {"start": v(-10.7, -10) * mm, "end": v(-10.86, -10.22) * mm});
            skLineSegment(sketch, "E748", {"start": v(-10.86, -10.22) * mm, "end": v(-11.2, -10.64) * mm});
            skLineSegment(sketch, "E749", {"start": v(-11.2, -10.64) * mm, "end": v(-11.56, -10.95) * mm});
            skLineSegment(sketch, "E750", {"start": v(-11.56, -10.95) * mm, "end": v(-11.67, -11.03) * mm});
            skLineSegment(sketch, "E751", {"start": v(-11.67, -11.03) * mm, "end": v(-12, -11.11) * mm});
            skLineSegment(sketch, "E752", {"start": v(-12, -11.11) * mm, "end": v(-12.15, -11.44) * mm});
            skLineSegment(sketch, "E753", {"start": v(-12.15, -11.44) * mm, "end": v(-12.22, -11.57) * mm});
            skLineSegment(sketch, "E754", {"start": v(-12.22, -11.57) * mm, "end": v(-12.3, -11.78) * mm});
            skLineSegment(sketch, "E755", {"start": v(-12.3, -11.78) * mm, "end": v(-12.42, -12.11) * mm});
            skLineSegment(sketch, "E756", {"start": v(-12.42, -12.11) * mm, "end": v(-12.44, -12.44) * mm});
            skLineSegment(sketch, "E757", {"start": v(-12.44, -12.44) * mm, "end": v(-12.22, -12.67) * mm});
            skLineSegment(sketch, "E758", {"start": v(-12.22, -12.67) * mm, "end": v(-11.89, -12.64) * mm});
            skLineSegment(sketch, "E759", {"start": v(-11.89, -12.64) * mm, "end": v(-11.54, -12.5) * mm});
            skLineSegment(sketch, "E760", {"start": v(-11.54, -12.5) * mm, "end": v(-11.11, -12.2) * mm});
            skLineSegment(sketch, "E761", {"start": v(-11.11, -12.2) * mm, "end": v(-10.89, -12) * mm});
            skLineSegment(sketch, "E762", {"start": v(-10.89, -12) * mm, "end": v(-10.44, -11.56) * mm});
            skLineSegment(sketch, "E763", {"start": v(-10.44, -11.56) * mm, "end": v(-10, -11.11) * mm});
            skLineSegment(sketch, "E764", {"start": v(-10, -11.11) * mm, "end": v(-9.78, -10.89) * mm});
            skLineSegment(sketch, "E765", {"start": v(-9.78, -10.89) * mm, "end": v(-9.57, -10.67) * mm});
            skLineSegment(sketch, "E766", {"start": v(-9.57, -10.67) * mm, "end": v(-9.2, -10.24) * mm});
            skLineSegment(sketch, "E767", {"start": v(-9.2, -10.24) * mm, "end": v(-9.04, -10.06) * mm});
            skLineSegment(sketch, "E768", {"start": v(-9.04, -10.06) * mm, "end": v(-8.76, -9.8) * mm});
            skLineSegment(sketch, "E769", {"start": v(-8.76, -9.8) * mm, "end": v(-8.44, -9.56) * mm});
            skLineSegment(sketch, "E770", {"start": v(-8.44, -9.56) * mm, "end": v(-8.44, -8.89) * mm});
            skLineSegment(sketch, "E771", {"start": v(-8.44, -8.89) * mm, "end": v(-8.67, -8.67) * mm});
            skLineSegment(sketch, "E772", {"start": v(-8.67, -8.67) * mm, "end": v(-9.33, -8.67) * mm});
            skLineSegment(sketch, "E773", {"start": v(8.67, -9.78) * mm, "end": v(9, -9.95) * mm});
            skLineSegment(sketch, "E774", {"start": v(9, -9.95) * mm, "end": v(9.12, -10.07) * mm});
            skLineSegment(sketch, "E775", {"start": v(9.12, -10.07) * mm, "end": v(9.35, -10.25) * mm});
            skLineSegment(sketch, "E776", {"start": v(9.35, -10.25) * mm, "end": v(9.56, -10.45) * mm});
            skLineSegment(sketch, "E777", {"start": v(9.56, -10.45) * mm, "end": v(9.78, -10.67) * mm});
            skLineSegment(sketch, "E778", {"start": v(9.78, -10.67) * mm, "end": v(10, -10.89) * mm});
            skLineSegment(sketch, "E779", {"start": v(10, -10.89) * mm, "end": v(10.44, -11.33) * mm});
            skLineSegment(sketch, "E780", {"start": v(10.44, -11.33) * mm, "end": v(10.89, -11.78) * mm});
            skLineSegment(sketch, "E781", {"start": v(10.89, -11.78) * mm, "end": v(11.11, -12) * mm});
            skLineSegment(sketch, "E782", {"start": v(11.11, -12) * mm, "end": v(11.33, -12.2) * mm});
            skLineSegment(sketch, "E783", {"start": v(11.33, -12.2) * mm, "end": v(11.77, -12.5) * mm});
            skLineSegment(sketch, "E784", {"start": v(11.77, -12.5) * mm, "end": v(12.11, -12.64) * mm});
            skLineSegment(sketch, "E785", {"start": v(12.11, -12.64) * mm, "end": v(12.44, -12.67) * mm});
            skLineSegment(sketch, "E786", {"start": v(12.44, -12.67) * mm, "end": v(12.67, -12.44) * mm});
            skLineSegment(sketch, "E787", {"start": v(12.67, -12.44) * mm, "end": v(12.64, -12.11) * mm});
            skLineSegment(sketch, "E788", {"start": v(12.64, -12.11) * mm, "end": v(12.5, -11.77) * mm});
            skLineSegment(sketch, "E789", {"start": v(12.5, -11.77) * mm, "end": v(12.2, -11.33) * mm});
            skLineSegment(sketch, "E790", {"start": v(12.2, -11.33) * mm, "end": v(12, -11.11) * mm});
            skLineSegment(sketch, "E791", {"start": v(12, -11.11) * mm, "end": v(11.78, -10.89) * mm});
            skLineSegment(sketch, "E792", {"start": v(11.78, -10.89) * mm, "end": v(11.33, -10.44) * mm});
            skLineSegment(sketch, "E793", {"start": v(11.33, -10.44) * mm, "end": v(10.89, -10) * mm});
            skLineSegment(sketch, "E794", {"start": v(10.89, -10) * mm, "end": v(10.67, -9.78) * mm});
            skLineSegment(sketch, "E795", {"start": v(10.67, -9.78) * mm, "end": v(10.22, -9.36) * mm});
            skLineSegment(sketch, "E796", {"start": v(10.22, -9.36) * mm, "end": v(9.78, -9.05) * mm});
            skLineSegment(sketch, "E797", {"start": v(9.78, -9.05) * mm, "end": v(9.56, -8.97) * mm});
            skLineSegment(sketch, "E798", {"start": v(9.56, -8.97) * mm, "end": v(9.34, -8.94) * mm});
            skLineSegment(sketch, "E799", {"start": v(9.34, -8.94) * mm, "end": v(9.14, -8.97) * mm});
            skLineSegment(sketch, "E800", {"start": v(9.14, -8.97) * mm, "end": v(8.83, -9.17) * mm});
            skLineSegment(sketch, "E801", {"start": v(8.83, -9.17) * mm, "end": v(8.74, -9.35) * mm});
            skLineSegment(sketch, "E802", {"start": v(8.74, -9.35) * mm, "end": v(8.67, -9.78) * mm});
            skLineSegment(sketch, "E803", {"start": v(-0.44, -9.11) * mm, "end": v(-0.44, -11.33) * mm});
            skLineSegment(sketch, "E804", {"start": v(-0.44, -11.33) * mm, "end": v(0.67, -11.33) * mm});
            skLineSegment(sketch, "E805", {"start": v(0.67, -11.33) * mm, "end": v(0.67, -9.11) * mm});
            skLineSegment(sketch, "E806", {"start": v(0.67, -9.11) * mm, "end": v(-0.44, -9.11) * mm});
            skLineSegment(sketch, "E807", {"start": v(-0.44, -12.44) * mm, "end": v(-0.44, -20) * mm});
            skLineSegment(sketch, "E808", {"start": v(-0.44, -20) * mm, "end": v(0.67, -20) * mm});
            skLineSegment(sketch, "E809", {"start": v(0.67, -20) * mm, "end": v(0.67, -12.44) * mm});
            skLineSegment(sketch, "E810", {"start": v(0.67, -12.44) * mm, "end": v(-0.44, -12.44) * mm});
            skSolve(sketch);
        }
        {
            var Q0;
            Q0=makeQuery(id+"F3.imprint","IMPRINT",FACE,{"disambiguationData":[TD([[makeQuery(id+"F3.imprint","IMPRINT",EDGE,{"derivedFrom":sQuery(id+"F3.wireOp",EDGE,"E326")}),1.0]])]});
            var Q1;
            Q1=makeQuery(id+"F3.imprint","IMPRINT",FACE,{"disambiguationData":[TD([[makeQuery(id+"F3.imprint","IMPRINT",EDGE,{"derivedFrom":sQuery(id+"F3.wireOp",EDGE,"E476")}),1.0]])]});
            var Q2;
            Q2=makeQuery(id+"F3.imprint","IMPRINT",FACE,{"disambiguationData":[TD([[makeQuery(id+"F3.imprint","IMPRINT",EDGE,{"derivedFrom":sQuery(id+"F3.wireOp",EDGE,"E741")}),1.0]])]});
            var Q3;
            Q3=makeQuery(id+"F3.imprint","IMPRINT",FACE,{"disambiguationData":[TD([[makeQuery(id+"F3.imprint","IMPRINT",EDGE,{"derivedFrom":sQuery(id+"F3.wireOp",EDGE,"E611")}),1.0]])]});
            var Q4;
            Q4=makeQuery(id+"F3.imprint","IMPRINT",FACE,{"disambiguationData":[TD([[makeQuery(id+"F3.imprint","IMPRINT",EDGE,{"derivedFrom":sQuery(id+"F3.wireOp",EDGE,"E627")}),1.0]])]});
            var Q5;
            Q5=makeQuery(id+"F3.imprint","IMPRINT",FACE,{"disambiguationData":[TD([[makeQuery(id+"F3.imprint","IMPRINT",EDGE,{"derivedFrom":sQuery(id+"F3.wireOp",EDGE,"E803")}),1.0]])]});
            var Q6;
            Q6=makeQuery(id+"F3.imprint","IMPRINT",FACE,{"disambiguationData":[TD([[makeQuery(id+"F3.imprint","IMPRINT",EDGE,{"derivedFrom":sQuery(id+"F3.wireOp",EDGE,"E807")}),1.0]])]});
            var Q7;
            Q7=makeQuery(id+"F3.imprint","IMPRINT",FACE,{"disambiguationData":[TD([[makeQuery(id+"F3.imprint","IMPRINT",EDGE,{"derivedFrom":sQuery(id+"F3.wireOp",EDGE,"E686")}),1.0]])]});
            var Q8;
            Q8=makeQuery(id+"F3.imprint","IMPRINT",FACE,{"disambiguationData":[TD([[makeQuery(id+"F3.imprint","IMPRINT",EDGE,{"derivedFrom":sQuery(id+"F3.wireOp",EDGE,"E592")}),1.0]])]});
            var Q9;
            Q9=makeQuery(id+"F3.imprint","IMPRINT",FACE,{"disambiguationData":[TD([[makeQuery(id+"F3.imprint","IMPRINT",EDGE,{"derivedFrom":sQuery(id+"F3.wireOp",EDGE,"E773")}),1.0]])]});
            var Q10;
            Q10=makeQuery(id+"F3.imprint","IMPRINT",FACE,{"disambiguationData":[TD([[makeQuery(id+"F3.imprint","IMPRINT",EDGE,{"derivedFrom":sQuery(id+"F3.wireOp",EDGE,"E534")}),1.0]])]});
            var Q11;
            Q11=makeQuery(id+"F3.imprint","IMPRINT",FACE,{"disambiguationData":[TD([[makeQuery(id+"F3.imprint","IMPRINT",EDGE,{"derivedFrom":sQuery(id+"F3.wireOp",EDGE,"E468")}),1.0]])]});
            var Q12;
            Q12=makeQuery(id+"F3.imprint","IMPRINT",FACE,{"disambiguationData":[TD([[makeQuery(id+"F3.imprint","IMPRINT",EDGE,{"derivedFrom":sQuery(id+"F3.wireOp",EDGE,"E472")}),1.0]])]});
            var Q13;
            Q13=makeQuery(id+"F3.imprint","IMPRINT",FACE,{"disambiguationData":[TD([[makeQuery(id+"F3.imprint","IMPRINT",EDGE,{"derivedFrom":sQuery(id+"F3.wireOp",EDGE,"E248")}),1.0]])]});
            var Q14;
            Q14=makeQuery(id+"F3.imprint","IMPRINT",FACE,{"disambiguationData":[TD([[makeQuery(id+"F3.imprint","IMPRINT",EDGE,{"derivedFrom":sQuery(id+"F3.wireOp",EDGE,"E309")}),1.0]])]});
            var Q15;
            Q15=makeQuery(id+"F3.imprint","IMPRINT",FACE,{"disambiguationData":[TD([[makeQuery(id+"F3.imprint","IMPRINT",EDGE,{"derivedFrom":sQuery(id+"F3.wireOp",EDGE,"E156")}),1.0]])]});
            var Q16;
            Q16=makeQuery(id+"F3.imprint","IMPRINT",FACE,{"disambiguationData":[TD([[makeQuery(id+"F3.imprint","IMPRINT",EDGE,{"derivedFrom":sQuery(id+"F3.wireOp",EDGE,"E10")}),1.0]])]});
            var Q17;
            Q17=makeQuery(id+"F3.imprint","IMPRINT",FACE,{"disambiguationData":[TD([[makeQuery(id+"F3.imprint","IMPRINT",EDGE,{"derivedFrom":sQuery(id+"F3.wireOp",EDGE,"E185")}),1.0]])]});
            var Q18;
            Q18=makeQuery(id+"F3.imprint","IMPRINT",FACE,{"disambiguationData":[TD([[makeQuery(id+"F3.imprint","IMPRINT",EDGE,{"derivedFrom":sQuery(id+"F3.wireOp",EDGE,"E6")}),1.0]])]});
            var Q19;
            Q19=makeQuery(id+"F3.imprint","IMPRINT",FACE,{"disambiguationData":[TD([[makeQuery(id+"F3.imprint","IMPRINT",EDGE,{"derivedFrom":sQuery(id+"F3.wireOp",EDGE,"E72")}),1.0]])]});
            var Q20;
            Q20=makeQuery(id+"F3.imprint","IMPRINT",FACE,{"disambiguationData":[TD([[makeQuery(id+"F3.imprint","IMPRINT",EDGE,{"derivedFrom":sQuery(id+"F3.wireOp",EDGE,"E294")}),1.0]])]});
            var Q21;
            Q21=makeQuery(id+"F3.imprint","IMPRINT",FACE,{"disambiguationData":[TD([[makeQuery(id+"F3.imprint","IMPRINT",EDGE,{"derivedFrom":sQuery(id+"F3.wireOp",EDGE,"E132")}),1.0]])]});
            var Q22;
            Q22=makeQuery(id+"F3.imprint","IMPRINT",FACE,{"disambiguationData":[TD([[makeQuery(id+"F3.imprint","IMPRINT",EDGE,{"derivedFrom":sQuery(id+"F3.wireOp",EDGE,"E190")}),1.0]])]});
            var Q23;
            Q23=makeQuery(id+"F3.imprint","IMPRINT",FACE,{"disambiguationData":[TD([[makeQuery(id+"F3.imprint","IMPRINT",EDGE,{"derivedFrom":sQuery(id+"F3.wireOp",EDGE,"E464")}),1.0]])]});
            var Q24;
            Q24=makeQuery(id+"F3.imprint","IMPRINT",FACE,{"disambiguationData":[TD([[makeQuery(id+"F3.imprint","IMPRINT",EDGE,{"derivedFrom":sQuery(id+"F3.wireOp",EDGE,"E460")}),1.0]])]});
            extrude(context, id + "F4", {"entities" : qUnion([Q0, Q1, Q2, Q3, Q4, Q5, Q6, Q7, Q8, Q9, Q10, Q11, Q12, Q13, Q14, Q15, Q16, Q17, Q18, Q19, Q20, Q21, Q22, Q23, Q24]), "operationType" : NewBodyOperationType.ADD, "depth" : 4 * mm});
        }
        {
            var Q0;
            Q0=makeQuery(id+"F1.opExtrude","SWEPT_BODY",BODY,{"disambiguationData":[OSD([sQuery(id+"F0.wireOp",EDGE,"E0"),sQuery(id+"F0.wireOp",EDGE,"E1"),sQuery(id+"F0.wireOp",EDGE,"E2"),sQuery(id+"F0.wireOp",EDGE,"E3"),sQuery(id+"F0.wireOp",EDGE,"E4"),sQuery(id+"F0.wireOp",EDGE,"E5.0")])]});
            var Q1;
            Q1=qCreatedBy(makeId("Origin.pointOp"),VERTEX);
            transform(context, id + "F5", {"entities" : qUnion([Q0]), "transformType" : TransformType.SCALE_UNIFORMLY, "scale" : 0.7, "scalePoint" : qUnion([Q1]), "makeCopy" : true});
        }
    });
